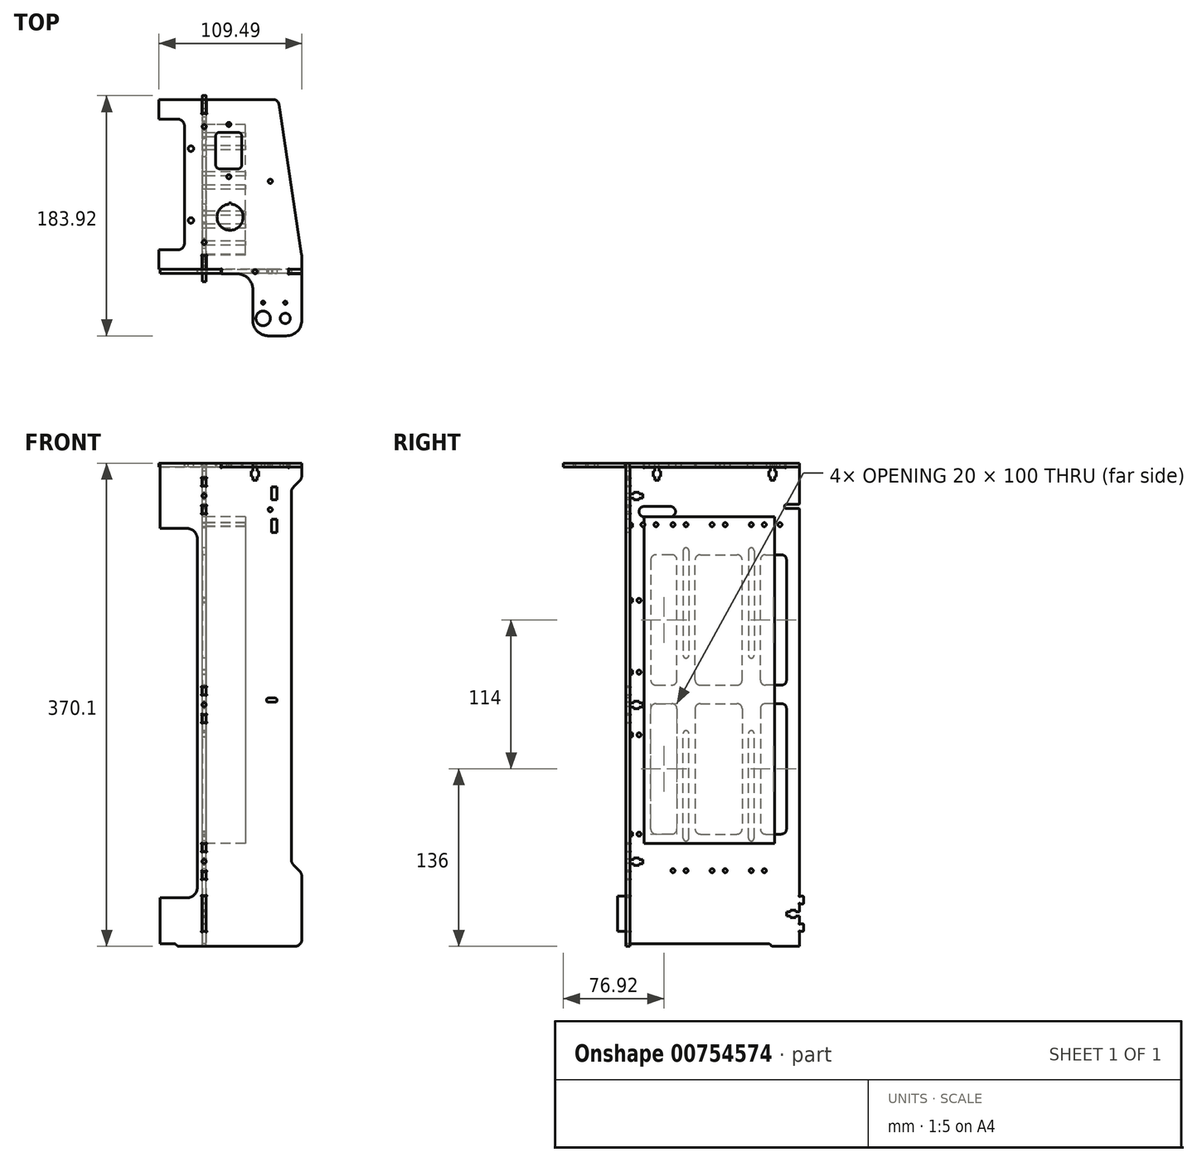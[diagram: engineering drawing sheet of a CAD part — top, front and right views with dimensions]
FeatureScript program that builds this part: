
annotation { "Feature Type Name" : "Feature", "Feature Type Description" : "" }
export const myFeature = defineFeature(function(context is Context, id is Id, definition is map)
    precondition{}
    {
        {
            assignVariable(context, id + "F0", {"name" : "profondeur_alim", "anyValue" : 30});
        }
        {
            var Q0;
            Q0=qCreatedBy(makeId("Top.planeOp"),FACE);
            var sketch = newSketch(context, id + "F1", { "sketchPlane" : qUnion([Q0])});
            skLineSegment(sketch, "E0", {"start": v(194.9, -37.1) * mm, "end": v(185.77, -37.1) * mm});
            skArc(sketch, "E1", {"start": v(185.33, -36.84) * mm, "mid": v(185.52, -37.03) * mm, "end": v(185.77, -37.1) * mm});
            skArc(sketch, "E2", {"start": v(185.33, -36.84) * mm, "mid": v(184.55, -36.74) * mm, "end": v(184.65, -37.53) * mm});
            skArc(sketch, "E3", {"start": v(184.9, -37.96) * mm, "mid": v(184.83, -37.71) * mm, "end": v(184.65, -37.53) * mm});
            skLineSegment(sketch, "E4", {"start": v(184.9, -37.96) * mm, "end": v(184.9, -39.53) * mm});
            skArc(sketch, "E5", {"start": v(184.65, -39.96) * mm, "mid": v(184.83, -39.78) * mm, "end": v(184.9, -39.53) * mm});
            skArc(sketch, "E6", {"start": v(184.65, -39.96) * mm, "mid": v(184.55, -40.75) * mm, "end": v(185.33, -40.64) * mm});
            skArc(sketch, "E7", {"start": v(185.77, -40.4) * mm, "mid": v(185.52, -40.46) * mm, "end": v(185.33, -40.64) * mm});
            skLineSegment(sketch, "E8", {"start": v(185.77, -40.4) * mm, "end": v(194.9, -40.4) * mm});
            skCircle(sketch, "E9", {"center": v(159.08, -38.74) * mm, "radius": 1.6 * mm});
            skLineSegment(sketch, "E10", {"start": v(133.25, -40.4) * mm, "end": v(133.25, -37.92) * mm});
            skArc(sketch, "E11", {"start": v(133.5, -37.48) * mm, "mid": v(133.32, -37.67) * mm, "end": v(133.25, -37.92) * mm});
            skArc(sketch, "E12", {"start": v(133.5, -37.48) * mm, "mid": v(133.6, -36.7) * mm, "end": v(132.82, -36.8) * mm});
            skArc(sketch, "E13", {"start": v(132.38, -37.05) * mm, "mid": v(132.63, -36.98) * mm, "end": v(132.82, -36.8) * mm});
            skLineSegment(sketch, "E14", {"start": v(132.38, -37.05) * mm, "end": v(121.73, -37.05) * mm});
            skLineSegment(sketch, "E15", {"start": v(121.73, -37.05) * mm, "end": v(121.73, -27.27) * mm});
            skArc(sketch, "E16", {"start": v(121.98, -26.83) * mm, "mid": v(121.8, -27.02) * mm, "end": v(121.73, -27.27) * mm});
            skArc(sketch, "E17", {"start": v(121.98, -26.83) * mm, "mid": v(122.08, -26.05) * mm, "end": v(121.3, -26.15) * mm});
            skArc(sketch, "E18", {"start": v(120.86, -26.4) * mm, "mid": v(121.1, -26.33) * mm, "end": v(121.3, -26.15) * mm});
            skLineSegment(sketch, "E19", {"start": v(120.86, -26.4) * mm, "end": v(119.3, -26.4) * mm});
            skArc(sketch, "E20", {"start": v(118.86, -26.15) * mm, "mid": v(119.04, -26.33) * mm, "end": v(119.3, -26.4) * mm});
            skArc(sketch, "E21", {"start": v(118.86, -26.15) * mm, "mid": v(118.07, -26.05) * mm, "end": v(118.18, -26.83) * mm});
            skArc(sketch, "E22", {"start": v(118.43, -27.27) * mm, "mid": v(118.36, -27.02) * mm, "end": v(118.18, -26.83) * mm});
            skLineSegment(sketch, "E23", {"start": v(118.43, -27.27) * mm, "end": v(118.43, -37.05) * mm});
            skCircle(sketch, "E24", {"center": v(120.08, -16.4) * mm, "radius": 1.6 * mm});
            skLineSegment(sketch, "E25", {"start": v(118.43, -37.05) * mm, "end": v(85.41, -37.05) * mm});
            skArc(sketch, "E26", {"start": v(99.9, -22.05) * mm, "mid": v(103.44, -20.58) * mm, "end": v(104.9, -17.05) * mm});
            skLineSegment(sketch, "E27", {"start": v(99.9, -22.05) * mm, "end": v(85.41, -22.05) * mm});
            skCircle(sketch, "E28", {"center": v(109.9, 0.45) * mm, "radius": 2.1 * mm});
            skLineSegment(sketch, "E29", {"start": v(194.9, -40.4) * mm, "end": v(194.9, -75.92) * mm});
            skArc(sketch, "E30", {"start": v(182.9, -87.92) * mm, "mid": v(191.39, -84.4) * mm, "end": v(194.9, -75.92) * mm});
            skCircle(sketch, "E31", {"center": v(182.2, -62.54) * mm, "radius": 1.25 * mm});
            skCircle(sketch, "E32", {"center": v(165.2, -74.55) * mm, "radius": 5.53 * mm});
            skCircle(sketch, "E33", {"center": v(165.2, -62.54) * mm, "radius": 1.25 * mm});
            skCircle(sketch, "E34", {"center": v(182.2, -74.54) * mm, "radius": 3.9 * mm});
            skLineSegment(sketch, "E35", {"start": v(194.9, -37.1) * mm, "end": v(194.9, -28.66) * mm});
            skArc(sketch, "E36", {"start": v(194.9, -28.66) * mm, "mid": v(194.84, -27.1) * mm, "end": v(194.66, -25.54) * mm});
            skCircle(sketch, "E37", {"center": v(120.08, 72.3) * mm, "radius": 1.6 * mm});
            skArc(sketch, "E38", {"start": v(104.9, 72.95) * mm, "mid": v(103.44, 76.49) * mm, "end": v(99.9, 77.95) * mm});
            skLineSegment(sketch, "E39", {"start": v(85.41, 77.95) * mm, "end": v(99.9, 77.95) * mm});
            skLineSegment(sketch, "E40", {"start": v(104.9, 72.95) * mm, "end": v(104.9, -17.05) * mm});
            skLineSegment(sketch, "E41", {"start": v(121.72, 92.95) * mm, "end": v(121.72, 83.17) * mm});
            skArc(sketch, "E42", {"start": v(121.72, 83.17) * mm, "mid": v(121.8, 82.92) * mm, "end": v(121.97, 82.73) * mm});
            skArc(sketch, "E43", {"start": v(121.3, 82.05) * mm, "mid": v(122.08, 81.95) * mm, "end": v(121.97, 82.73) * mm});
            skArc(sketch, "E44", {"start": v(121.3, 82.05) * mm, "mid": v(121.1, 82.23) * mm, "end": v(120.86, 82.3) * mm});
            skLineSegment(sketch, "E45", {"start": v(120.86, 82.3) * mm, "end": v(119.3, 82.3) * mm});
            skArc(sketch, "E46", {"start": v(119.3, 82.3) * mm, "mid": v(119.04, 82.23) * mm, "end": v(118.86, 82.05) * mm});
            skArc(sketch, "E47", {"start": v(118.17, 82.74) * mm, "mid": v(118.07, 81.95) * mm, "end": v(118.86, 82.05) * mm});
            skArc(sketch, "E48", {"start": v(118.17, 82.74) * mm, "mid": v(118.36, 82.92) * mm, "end": v(118.42, 83.17) * mm});
            skLineSegment(sketch, "E49", {"start": v(118.42, 83.17) * mm, "end": v(118.42, 92.95) * mm});
            skLineSegment(sketch, "E50", {"start": v(118.42, 92.95) * mm, "end": v(85.41, 92.95) * mm});
            skLineSegment(sketch, "E51", {"start": v(173.3, 92.95) * mm, "end": v(121.72, 92.95) * mm});
            skArc(sketch, "E52", {"start": v(177.26, 89.57) * mm, "mid": v(175.9, 92) * mm, "end": v(173.3, 92.95) * mm});
            skLineSegment(sketch, "E53", {"start": v(194.66, -25.54) * mm, "end": v(177.26, 89.57) * mm});
            skCircle(sketch, "E54", {"center": v(109.9, 55.45) * mm, "radius": 2.1 * mm});
            skArc(sketch, "E55", {"start": v(157.3, -52.4) * mm, "mid": v(153.78, -43.91) * mm, "end": v(145.29, -40.4) * mm});
            skArc(sketch, "E56", {"start": v(157.3, -75.92) * mm, "mid": v(160.8, -84.4) * mm, "end": v(169.3, -87.92) * mm});
            skLineSegment(sketch, "E57", {"start": v(157.3, -52.4) * mm, "end": v(157.3, -75.92) * mm});
            skLineSegment(sketch, "E58", {"start": v(145.29, -40.4) * mm, "end": v(133.25, -40.4) * mm});
            skLineSegment(sketch, "E59", {"start": v(169.3, -87.92) * mm, "end": v(182.9, -87.92) * mm});
            skCircle(sketch, "E60", {"center": v(138.87, 33.99) * mm, "radius": 1.6 * mm});
            skArc(sketch, "E61", {"start": v(145.87, 39.99) * mm, "mid": v(148, 40.87) * mm, "end": v(148.87, 42.99) * mm});
            skLineSegment(sketch, "E62", {"start": v(145.87, 39.99) * mm, "end": v(131.87, 39.99) * mm});
            skArc(sketch, "E63", {"start": v(128.87, 42.99) * mm, "mid": v(129.75, 40.87) * mm, "end": v(131.87, 39.99) * mm});
            skLineSegment(sketch, "E64", {"start": v(128.87, 64.99) * mm, "end": v(128.87, 42.99) * mm});
            skArc(sketch, "E65", {"start": v(131.87, 67.99) * mm, "mid": v(129.75, 67.1) * mm, "end": v(128.87, 64.99) * mm});
            skLineSegment(sketch, "E66", {"start": v(145.87, 67.99) * mm, "end": v(131.87, 67.99) * mm});
            skArc(sketch, "E67", {"start": v(148.87, 64.99) * mm, "mid": v(148, 67.1) * mm, "end": v(145.87, 67.99) * mm});
            skLineSegment(sketch, "E68", {"start": v(148.87, 64.99) * mm, "end": v(148.87, 42.99) * mm});
            skCircle(sketch, "E69", {"center": v(138.87, 73.99) * mm, "radius": 1.6 * mm});
            skArc(sketch, "E70", {"start": v(138.8, 12.89) * mm, "mid": v(139.9, -7.05) * mm, "end": v(141, 12.89) * mm});
            skLineSegment(sketch, "E71", {"start": v(141, 13.95) * mm, "end": v(141, 12.9) * mm});
            skLineSegment(sketch, "E72", {"start": v(138.8, 13.95) * mm, "end": v(138.8, 12.9) * mm});
            skLineSegment(sketch, "E73", {"start": v(138.8, 13.95) * mm, "end": v(141, 13.95) * mm});
            skCircle(sketch, "E74", {"center": v(170.72, 30.45) * mm, "radius": 1.6 * mm});
            skLineSegment(sketch, "E75", {"start": v(85.41, -37.05) * mm, "end": v(85.41, -22.05) * mm});
            skLineSegment(sketch, "E76", {"start": v(76.17, 13.3) * mm, "end": v(24.44, 13.3) * mm, "construction": true});
            skPoint(sketch, "E77.end.orphan", {"position": v(52.4, -36.45) * mm});
            skLineSegment(sketch, "E78.trimOffspring", {"start": v(85.41, 77.95) * mm, "end": v(85.41, 92.95) * mm});
            skSolve(sketch);
        }
        {
            var Q0;
            Q0=makeQuery(id+"F1.imprint","IMPRINT",FACE,{"disambiguationData":[TD([[makeQuery(id+"F1.imprint","IMPRINT",EDGE,{"derivedFrom":sQuery(id+"F1.wireOp",EDGE,"E0")}),-1.0]])]});
            extrude(context, id + "F2", {"entities" : qUnion([Q0]), "oppositeDirection" : true, "depth" : 3 * mm, "offsetDistance" : 25 * mm});
        }
        {
            var Q0;
            Q0=qCreatedBy(makeId("Front.planeOp"),FACE);
            cPlane(context, id + "F3", {"entities" : qUnion([Q0]), "cplaneType" : CPlaneType.OFFSET, "offset" : 40 * mm, "width" : 150 * mm, "height" : 150 * mm});
        }
        {
            var Q0;
            Q0=qCreatedBy(id+"F3.planeOp",FACE);
            var sketch = newSketch(context, id + "F4", { "sketchPlane" : qUnion([Q0])});
            skArc(sketch, "E79", {"start": v(189.8, -369.9) * mm, "mid": v(193.34, -368.44) * mm, "end": v(194.8, -364.9) * mm});
            skLineSegment(sketch, "E80", {"start": v(194.8, 0.1) * mm, "end": v(184.8, 0.1) * mm});
            skLineSegment(sketch, "E81", {"start": v(184.8, 0.1) * mm, "end": v(184.8, -2.13) * mm});
            skArc(sketch, "E82", {"start": v(184.8, -2.13) * mm, "mid": v(184.87, -2.38) * mm, "end": v(185.06, -2.57) * mm});
            skArc(sketch, "E83", {"start": v(184.37, -3.25) * mm, "mid": v(185.16, -3.35) * mm, "end": v(185.06, -2.57) * mm});
            skArc(sketch, "E84", {"start": v(184.37, -3.25) * mm, "mid": v(184.19, -3.07) * mm, "end": v(183.94, -3) * mm});
            skLineSegment(sketch, "E85", {"start": v(183.94, -3) * mm, "end": v(160.58, -3) * mm});
            skLineSegment(sketch, "E86", {"start": v(160.58, -3) * mm, "end": v(160.58, -6) * mm});
            skLineSegment(sketch, "E87", {"start": v(160.58, -6) * mm, "end": v(161.86, -6) * mm});
            skLineSegment(sketch, "E88", {"start": v(161.86, -6) * mm, "end": v(161.86, -10) * mm});
            skLineSegment(sketch, "E89", {"start": v(161.86, -10) * mm, "end": v(160.58, -10) * mm});
            skLineSegment(sketch, "E90", {"start": v(160.58, -10) * mm, "end": v(160.58, -13) * mm});
            skLineSegment(sketch, "E91", {"start": v(160.58, -13) * mm, "end": v(157.38, -13) * mm});
            skLineSegment(sketch, "E92", {"start": v(157.38, -13) * mm, "end": v(157.38, -10) * mm});
            skLineSegment(sketch, "E93", {"start": v(157.38, -10) * mm, "end": v(156.1, -10) * mm});
            skLineSegment(sketch, "E94", {"start": v(156.1, -10) * mm, "end": v(156.1, -6) * mm});
            skLineSegment(sketch, "E95", {"start": v(156.1, -6) * mm, "end": v(157.38, -6) * mm});
            skLineSegment(sketch, "E96", {"start": v(157.38, -6) * mm, "end": v(157.38, -3) * mm});
            skLineSegment(sketch, "E97", {"start": v(106.8, -49.9) * mm, "end": v(86.12, -49.9) * mm});
            skArc(sketch, "E98", {"start": v(120.76, -331.2) * mm, "mid": v(121.01, -331.13) * mm, "end": v(121.2, -330.95) * mm});
            skArc(sketch, "E99", {"start": v(121.88, -331.63) * mm, "mid": v(121.98, -330.85) * mm, "end": v(121.2, -330.95) * mm});
            skArc(sketch, "E100", {"start": v(121.88, -331.63) * mm, "mid": v(121.7, -331.82) * mm, "end": v(121.63, -332.07) * mm});
            skLineSegment(sketch, "E101", {"start": v(121.63, -332.07) * mm, "end": v(121.63, -357.73) * mm});
            skArc(sketch, "E102", {"start": v(121.63, -357.73) * mm, "mid": v(121.7, -357.98) * mm, "end": v(121.88, -358.17) * mm});
            skArc(sketch, "E103", {"start": v(121.2, -358.85) * mm, "mid": v(121.98, -358.95) * mm, "end": v(121.88, -358.17) * mm});
            skArc(sketch, "E104", {"start": v(121.2, -358.85) * mm, "mid": v(121.01, -358.67) * mm, "end": v(120.76, -358.6) * mm});
            skLineSegment(sketch, "E105", {"start": v(120.76, -358.6) * mm, "end": v(119.2, -358.6) * mm});
            skArc(sketch, "E106", {"start": v(119.2, -358.6) * mm, "mid": v(118.95, -358.67) * mm, "end": v(118.76, -358.85) * mm});
            skArc(sketch, "E107", {"start": v(118.08, -358.17) * mm, "mid": v(117.98, -358.95) * mm, "end": v(118.76, -358.85) * mm});
            skArc(sketch, "E108", {"start": v(118.08, -358.17) * mm, "mid": v(118.26, -357.98) * mm, "end": v(118.33, -357.73) * mm});
            skLineSegment(sketch, "E109", {"start": v(118.33, -357.73) * mm, "end": v(118.33, -332.07) * mm});
            skArc(sketch, "E110", {"start": v(118.33, -332.07) * mm, "mid": v(118.26, -331.82) * mm, "end": v(118.08, -331.63) * mm});
            skArc(sketch, "E111", {"start": v(118.76, -330.95) * mm, "mid": v(117.98, -330.85) * mm, "end": v(118.08, -331.63) * mm});
            skArc(sketch, "E112", {"start": v(118.76, -330.95) * mm, "mid": v(118.95, -331.13) * mm, "end": v(119.2, -331.2) * mm});
            skLineSegment(sketch, "E113", {"start": v(119.2, -331.2) * mm, "end": v(120.76, -331.2) * mm});
            skArc(sketch, "E114", {"start": v(118.76, -312.15) * mm, "mid": v(118.95, -312.33) * mm, "end": v(119.2, -312.4) * mm});
            skArc(sketch, "E115", {"start": v(118.76, -312.15) * mm, "mid": v(117.98, -312.05) * mm, "end": v(118.08, -312.83) * mm});
            skArc(sketch, "E116", {"start": v(118.33, -313.27) * mm, "mid": v(118.26, -313.02) * mm, "end": v(118.08, -312.83) * mm});
            skLineSegment(sketch, "E117", {"start": v(118.33, -313.27) * mm, "end": v(118.33, -317.73) * mm});
            skArc(sketch, "E118", {"start": v(118.08, -318.17) * mm, "mid": v(118.26, -317.98) * mm, "end": v(118.33, -317.73) * mm});
            skArc(sketch, "E119", {"start": v(118.08, -318.17) * mm, "mid": v(117.98, -318.95) * mm, "end": v(118.76, -318.85) * mm});
            skArc(sketch, "E120", {"start": v(119.2, -318.6) * mm, "mid": v(118.95, -318.67) * mm, "end": v(118.76, -318.85) * mm});
            skLineSegment(sketch, "E121", {"start": v(119.2, -318.6) * mm, "end": v(120.76, -318.6) * mm});
            skArc(sketch, "E122", {"start": v(121.2, -318.85) * mm, "mid": v(121.01, -318.67) * mm, "end": v(120.76, -318.6) * mm});
            skArc(sketch, "E123", {"start": v(121.2, -318.85) * mm, "mid": v(121.98, -318.95) * mm, "end": v(121.88, -318.17) * mm});
            skArc(sketch, "E124", {"start": v(121.63, -317.73) * mm, "mid": v(121.7, -317.98) * mm, "end": v(121.88, -318.17) * mm});
            skLineSegment(sketch, "E125", {"start": v(121.63, -317.73) * mm, "end": v(121.63, -313.27) * mm});
            skArc(sketch, "E126", {"start": v(121.88, -312.83) * mm, "mid": v(121.7, -313.02) * mm, "end": v(121.63, -313.27) * mm});
            skArc(sketch, "E127", {"start": v(121.88, -312.83) * mm, "mid": v(121.98, -312.05) * mm, "end": v(121.2, -312.15) * mm});
            skArc(sketch, "E128", {"start": v(120.76, -312.4) * mm, "mid": v(121.01, -312.33) * mm, "end": v(121.2, -312.15) * mm});
            skLineSegment(sketch, "E129", {"start": v(120.76, -312.4) * mm, "end": v(119.2, -312.4) * mm});
            skArc(sketch, "E130", {"start": v(118.76, -290.95) * mm, "mid": v(118.95, -291.13) * mm, "end": v(119.2, -291.2) * mm});
            skArc(sketch, "E131", {"start": v(118.76, -290.95) * mm, "mid": v(117.98, -290.85) * mm, "end": v(118.08, -291.63) * mm});
            skArc(sketch, "E132", {"start": v(118.33, -292.07) * mm, "mid": v(118.26, -291.82) * mm, "end": v(118.08, -291.63) * mm});
            skLineSegment(sketch, "E133", {"start": v(118.33, -292.07) * mm, "end": v(118.33, -296.53) * mm});
            skArc(sketch, "E134", {"start": v(118.08, -296.97) * mm, "mid": v(118.26, -296.78) * mm, "end": v(118.33, -296.53) * mm});
            skArc(sketch, "E135", {"start": v(118.08, -296.97) * mm, "mid": v(117.98, -297.75) * mm, "end": v(118.76, -297.65) * mm});
            skArc(sketch, "E136", {"start": v(119.2, -297.4) * mm, "mid": v(118.95, -297.47) * mm, "end": v(118.76, -297.65) * mm});
            skLineSegment(sketch, "E137", {"start": v(119.2, -297.4) * mm, "end": v(120.76, -297.4) * mm});
            skArc(sketch, "E138", {"start": v(121.2, -297.65) * mm, "mid": v(121.01, -297.47) * mm, "end": v(120.76, -297.4) * mm});
            skArc(sketch, "E139", {"start": v(121.2, -297.65) * mm, "mid": v(121.98, -297.75) * mm, "end": v(121.88, -296.97) * mm});
            skArc(sketch, "E140", {"start": v(121.63, -296.53) * mm, "mid": v(121.7, -296.78) * mm, "end": v(121.88, -296.97) * mm});
            skLineSegment(sketch, "E141", {"start": v(121.63, -296.53) * mm, "end": v(121.63, -292.07) * mm});
            skArc(sketch, "E142", {"start": v(121.88, -291.63) * mm, "mid": v(121.7, -291.82) * mm, "end": v(121.63, -292.07) * mm});
            skArc(sketch, "E143", {"start": v(121.88, -291.63) * mm, "mid": v(121.98, -290.85) * mm, "end": v(121.2, -290.95) * mm});
            skArc(sketch, "E144", {"start": v(120.76, -291.2) * mm, "mid": v(121.01, -291.13) * mm, "end": v(121.2, -290.95) * mm});
            skLineSegment(sketch, "E145", {"start": v(120.76, -291.2) * mm, "end": v(119.2, -291.2) * mm});
            skArc(sketch, "E146", {"start": v(120.76, -192.4) * mm, "mid": v(121.01, -192.33) * mm, "end": v(121.2, -192.15) * mm});
            skArc(sketch, "E147", {"start": v(121.88, -192.83) * mm, "mid": v(121.98, -192.05) * mm, "end": v(121.2, -192.15) * mm});
            skArc(sketch, "E148", {"start": v(121.88, -192.83) * mm, "mid": v(121.7, -193.02) * mm, "end": v(121.63, -193.27) * mm});
            skLineSegment(sketch, "E149", {"start": v(121.63, -193.27) * mm, "end": v(121.63, -197.73) * mm});
            skArc(sketch, "E150", {"start": v(121.63, -197.73) * mm, "mid": v(121.7, -197.98) * mm, "end": v(121.88, -198.17) * mm});
            skArc(sketch, "E151", {"start": v(121.2, -198.85) * mm, "mid": v(121.98, -198.95) * mm, "end": v(121.88, -198.17) * mm});
            skArc(sketch, "E152", {"start": v(121.2, -198.85) * mm, "mid": v(121.01, -198.67) * mm, "end": v(120.76, -198.6) * mm});
            skLineSegment(sketch, "E153", {"start": v(120.76, -198.6) * mm, "end": v(119.2, -198.6) * mm});
            skArc(sketch, "E154", {"start": v(119.2, -198.6) * mm, "mid": v(118.95, -198.67) * mm, "end": v(118.76, -198.85) * mm});
            skArc(sketch, "E155", {"start": v(118.08, -198.17) * mm, "mid": v(117.98, -198.95) * mm, "end": v(118.76, -198.85) * mm});
            skArc(sketch, "E156", {"start": v(118.08, -198.17) * mm, "mid": v(118.26, -197.98) * mm, "end": v(118.33, -197.73) * mm});
            skLineSegment(sketch, "E157", {"start": v(118.33, -197.73) * mm, "end": v(118.33, -193.27) * mm});
            skArc(sketch, "E158", {"start": v(118.33, -193.27) * mm, "mid": v(118.26, -193.02) * mm, "end": v(118.08, -192.83) * mm});
            skArc(sketch, "E159", {"start": v(118.76, -192.15) * mm, "mid": v(117.98, -192.05) * mm, "end": v(118.08, -192.83) * mm});
            skArc(sketch, "E160", {"start": v(118.76, -192.15) * mm, "mid": v(118.95, -192.33) * mm, "end": v(119.2, -192.4) * mm});
            skLineSegment(sketch, "E161", {"start": v(119.2, -192.4) * mm, "end": v(120.76, -192.4) * mm});
            skArc(sketch, "E162", {"start": v(120.76, -171.2) * mm, "mid": v(121.01, -171.13) * mm, "end": v(121.2, -170.95) * mm});
            skArc(sketch, "E163", {"start": v(121.88, -171.63) * mm, "mid": v(121.98, -170.85) * mm, "end": v(121.2, -170.95) * mm});
            skArc(sketch, "E164", {"start": v(121.88, -171.63) * mm, "mid": v(121.7, -171.82) * mm, "end": v(121.63, -172.07) * mm});
            skLineSegment(sketch, "E165", {"start": v(121.63, -172.07) * mm, "end": v(121.63, -176.53) * mm});
            skArc(sketch, "E166", {"start": v(121.63, -176.53) * mm, "mid": v(121.7, -176.78) * mm, "end": v(121.88, -176.97) * mm});
            skArc(sketch, "E167", {"start": v(121.2, -177.65) * mm, "mid": v(121.98, -177.75) * mm, "end": v(121.88, -176.97) * mm});
            skArc(sketch, "E168", {"start": v(121.2, -177.65) * mm, "mid": v(121.01, -177.47) * mm, "end": v(120.76, -177.4) * mm});
            skLineSegment(sketch, "E169", {"start": v(120.76, -177.4) * mm, "end": v(119.2, -177.4) * mm});
            skArc(sketch, "E170", {"start": v(119.2, -177.4) * mm, "mid": v(118.95, -177.47) * mm, "end": v(118.76, -177.65) * mm});
            skArc(sketch, "E171", {"start": v(118.08, -176.97) * mm, "mid": v(117.98, -177.75) * mm, "end": v(118.76, -177.65) * mm});
            skArc(sketch, "E172", {"start": v(118.08, -176.97) * mm, "mid": v(118.26, -176.78) * mm, "end": v(118.33, -176.53) * mm});
            skLineSegment(sketch, "E173", {"start": v(118.33, -176.53) * mm, "end": v(118.33, -172.07) * mm});
            skArc(sketch, "E174", {"start": v(118.33, -172.07) * mm, "mid": v(118.26, -171.82) * mm, "end": v(118.08, -171.63) * mm});
            skArc(sketch, "E175", {"start": v(118.76, -170.95) * mm, "mid": v(117.98, -170.85) * mm, "end": v(118.08, -171.63) * mm});
            skArc(sketch, "E176", {"start": v(118.76, -170.95) * mm, "mid": v(118.95, -171.13) * mm, "end": v(119.2, -171.2) * mm});
            skLineSegment(sketch, "E177", {"start": v(119.2, -171.2) * mm, "end": v(120.76, -171.2) * mm});
            skArc(sketch, "E178", {"start": v(120.76, -32.4) * mm, "mid": v(121.01, -32.33) * mm, "end": v(121.2, -32.15) * mm});
            skArc(sketch, "E179", {"start": v(121.88, -32.83) * mm, "mid": v(121.98, -32.05) * mm, "end": v(121.2, -32.15) * mm});
            skArc(sketch, "E180", {"start": v(121.88, -32.83) * mm, "mid": v(121.7, -33.02) * mm, "end": v(121.63, -33.27) * mm});
            skLineSegment(sketch, "E181", {"start": v(121.63, -33.27) * mm, "end": v(121.63, -37.73) * mm});
            skArc(sketch, "E182", {"start": v(121.63, -37.73) * mm, "mid": v(121.7, -37.98) * mm, "end": v(121.88, -38.17) * mm});
            skArc(sketch, "E183", {"start": v(121.2, -38.85) * mm, "mid": v(121.98, -38.95) * mm, "end": v(121.88, -38.17) * mm});
            skArc(sketch, "E184", {"start": v(121.2, -38.85) * mm, "mid": v(121.01, -38.67) * mm, "end": v(120.76, -38.6) * mm});
            skLineSegment(sketch, "E185", {"start": v(120.76, -38.6) * mm, "end": v(119.2, -38.6) * mm});
            skArc(sketch, "E186", {"start": v(119.2, -38.6) * mm, "mid": v(118.95, -38.67) * mm, "end": v(118.76, -38.85) * mm});
            skArc(sketch, "E187", {"start": v(118.08, -38.17) * mm, "mid": v(117.98, -38.95) * mm, "end": v(118.76, -38.85) * mm});
            skArc(sketch, "E188", {"start": v(118.08, -38.17) * mm, "mid": v(118.26, -37.98) * mm, "end": v(118.33, -37.73) * mm});
            skLineSegment(sketch, "E189", {"start": v(118.33, -37.73) * mm, "end": v(118.33, -33.27) * mm});
            skArc(sketch, "E190", {"start": v(118.33, -33.27) * mm, "mid": v(118.26, -33.02) * mm, "end": v(118.08, -32.83) * mm});
            skArc(sketch, "E191", {"start": v(118.76, -32.15) * mm, "mid": v(117.98, -32.05) * mm, "end": v(118.08, -32.83) * mm});
            skArc(sketch, "E192", {"start": v(118.76, -32.15) * mm, "mid": v(118.95, -32.33) * mm, "end": v(119.2, -32.4) * mm});
            skLineSegment(sketch, "E193", {"start": v(119.2, -32.4) * mm, "end": v(120.76, -32.4) * mm});
            skArc(sketch, "E194", {"start": v(120.76, -11.2) * mm, "mid": v(121.01, -11.13) * mm, "end": v(121.2, -10.95) * mm});
            skArc(sketch, "E195", {"start": v(121.88, -11.63) * mm, "mid": v(121.98, -10.85) * mm, "end": v(121.2, -10.95) * mm});
            skArc(sketch, "E196", {"start": v(121.88, -11.63) * mm, "mid": v(121.7, -11.82) * mm, "end": v(121.63, -12.07) * mm});
            skLineSegment(sketch, "E197", {"start": v(121.63, -12.07) * mm, "end": v(121.63, -16.53) * mm});
            skArc(sketch, "E198", {"start": v(121.63, -16.53) * mm, "mid": v(121.7, -16.78) * mm, "end": v(121.88, -16.97) * mm});
            skArc(sketch, "E199", {"start": v(121.2, -17.65) * mm, "mid": v(121.98, -17.75) * mm, "end": v(121.88, -16.97) * mm});
            skArc(sketch, "E200", {"start": v(121.2, -17.65) * mm, "mid": v(121.01, -17.47) * mm, "end": v(120.76, -17.4) * mm});
            skLineSegment(sketch, "E201", {"start": v(120.76, -17.4) * mm, "end": v(119.2, -17.4) * mm});
            skArc(sketch, "E202", {"start": v(119.2, -17.4) * mm, "mid": v(118.95, -17.47) * mm, "end": v(118.76, -17.65) * mm});
            skArc(sketch, "E203", {"start": v(118.08, -16.97) * mm, "mid": v(117.98, -17.75) * mm, "end": v(118.76, -17.65) * mm});
            skArc(sketch, "E204", {"start": v(118.08, -16.97) * mm, "mid": v(118.26, -16.78) * mm, "end": v(118.33, -16.53) * mm});
            skLineSegment(sketch, "E205", {"start": v(118.33, -16.53) * mm, "end": v(118.33, -12.07) * mm});
            skArc(sketch, "E206", {"start": v(118.33, -12.07) * mm, "mid": v(118.26, -11.82) * mm, "end": v(118.08, -11.63) * mm});
            skArc(sketch, "E207", {"start": v(118.76, -10.95) * mm, "mid": v(117.98, -10.85) * mm, "end": v(118.08, -11.63) * mm});
            skArc(sketch, "E208", {"start": v(118.76, -10.95) * mm, "mid": v(118.95, -11.13) * mm, "end": v(119.2, -11.2) * mm});
            skLineSegment(sketch, "E209", {"start": v(119.2, -11.2) * mm, "end": v(120.76, -11.2) * mm});
            skCircle(sketch, "E210", {"center": v(119.98, -304.9) * mm, "radius": 1.6 * mm});
            skCircle(sketch, "E211", {"center": v(119.98, -184.9) * mm, "radius": 1.6 * mm});
            skCircle(sketch, "E212", {"center": v(119.98, -24.9) * mm, "radius": 1.6 * mm});
            skLineSegment(sketch, "E213", {"start": v(114.8, -324.8) * mm, "end": v(114.8, -57.9) * mm});
            skArc(sketch, "E214", {"start": v(106.8, -332.78) * mm, "mid": v(112.46, -330.44) * mm, "end": v(114.8, -324.8) * mm});
            skLineSegment(sketch, "E215", {"start": v(133, 0.1) * mm, "end": v(86.12, 0.1) * mm});
            skArc(sketch, "E216", {"start": v(133.87, -3) * mm, "mid": v(133.62, -3.07) * mm, "end": v(133.44, -3.25) * mm});
            skArc(sketch, "E217", {"start": v(132.76, -2.57) * mm, "mid": v(132.65, -3.35) * mm, "end": v(133.44, -3.25) * mm});
            skArc(sketch, "E218", {"start": v(132.76, -2.57) * mm, "mid": v(132.94, -2.38) * mm, "end": v(133, -2.13) * mm});
            skLineSegment(sketch, "E219", {"start": v(133, -2.13) * mm, "end": v(133, 0.1) * mm});
            skLineSegment(sketch, "E220", {"start": v(157.38, -3) * mm, "end": v(133.87, -3) * mm});
            skLineSegment(sketch, "E221", {"start": v(194.8, -364.9) * mm, "end": v(194.8, -316.36) * mm});
            skArc(sketch, "E222", {"start": v(194.8, -316.36) * mm, "mid": v(194.36, -314.09) * mm, "end": v(193.07, -312.15) * mm});
            skLineSegment(sketch, "E223", {"start": v(188.54, -307.56) * mm, "end": v(193.07, -312.15) * mm});
            skArc(sketch, "E224", {"start": v(186.8, -303.34) * mm, "mid": v(187.26, -305.62) * mm, "end": v(188.54, -307.56) * mm});
            skLineSegment(sketch, "E225", {"start": v(194.8, -9.42) * mm, "end": v(194.8, 0.1) * mm});
            skArc(sketch, "E226", {"start": v(193.05, -13.66) * mm, "mid": v(194.35, -11.71) * mm, "end": v(194.8, -9.42) * mm});
            skLineSegment(sketch, "E227", {"start": v(193.05, -13.66) * mm, "end": v(188.56, -18.14) * mm});
            skArc(sketch, "E228", {"start": v(188.56, -18.14) * mm, "mid": v(187.26, -20.09) * mm, "end": v(186.8, -22.39) * mm});
            skLineSegment(sketch, "E229", {"start": v(106.8, -332.78) * mm, "end": v(86.12, -332.78) * mm});
            skArc(sketch, "E230", {"start": v(98.1, -368.2) * mm, "mid": v(97.77, -367.98) * mm, "end": v(97.4, -367.9) * mm});
            skLineSegment(sketch, "E231", {"start": v(189.8, -369.9) * mm, "end": v(100.22, -369.9) * mm});
            skLineSegment(sketch, "E232", {"start": v(98.1, -368.2) * mm, "end": v(99.51, -369.6) * mm});
            skArc(sketch, "E233", {"start": v(99.51, -369.6) * mm, "mid": v(99.84, -369.82) * mm, "end": v(100.22, -369.9) * mm});
            skArc(sketch, "E234", {"start": v(174.3, -183) * mm, "mid": v(175.9, -181.4) * mm, "end": v(174.3, -179.8) * mm});
            skArc(sketch, "E235", {"start": v(169.3, -179.8) * mm, "mid": v(167.7, -181.4) * mm, "end": v(169.3, -183) * mm});
            skLineSegment(sketch, "E236", {"start": v(174.3, -179.8) * mm, "end": v(169.3, -179.8) * mm});
            skLineSegment(sketch, "E237", {"start": v(174.3, -183) * mm, "end": v(169.3, -183) * mm});
            skLineSegment(sketch, "E238", {"start": v(186.8, -22.39) * mm, "end": v(186.8, -303.34) * mm});
            skLineSegment(sketch, "E239", {"start": v(171.63, -28) * mm, "end": v(171.63, -18) * mm});
            skLineSegment(sketch, "E240", {"start": v(171.63, -18) * mm, "end": v(175.63, -18) * mm});
            skLineSegment(sketch, "E241", {"start": v(175.63, -18) * mm, "end": v(175.63, -28) * mm});
            skLineSegment(sketch, "E242", {"start": v(175.63, -28) * mm, "end": v(171.63, -28) * mm});
            skLineSegment(sketch, "E243", {"start": v(171.63, -53) * mm, "end": v(171.63, -43) * mm});
            skLineSegment(sketch, "E244", {"start": v(171.63, -43) * mm, "end": v(175.63, -43) * mm});
            skLineSegment(sketch, "E245", {"start": v(175.63, -43) * mm, "end": v(175.63, -53) * mm});
            skLineSegment(sketch, "E246", {"start": v(175.63, -53) * mm, "end": v(171.63, -53) * mm});
            skCircle(sketch, "E247", {"center": v(170.63, -35.5) * mm, "radius": 1.6 * mm});
            skPoint(sketch, "E248.end.orphan", {"position": v(-11.92, 174.3) * mm});
            skPoint(sketch, "E249.end.orphan", {"position": v(92.12, 0.1) * mm});
            skLineSegment(sketch, "E250", {"start": v(86.12, -367.9) * mm, "end": v(97.4, -367.9) * mm});
            skLineSegment(sketch, "E251", {"start": v(86.12, -367.9) * mm, "end": v(86.12, -332.78) * mm});
            skPoint(sketch, "E252.orphan", {"position": v(125.38, -49.9) * mm});
            skLineSegment(sketch, "E253", {"start": v(86.12, -49.9) * mm, "end": v(86.12, 0.1) * mm});
            skPoint(sketch, "E254.end.orphan", {"position": v(96.46, -49.9) * mm});
            skArc(sketch, "E255", {"start": v(114.8, -57.9) * mm, "mid": v(112.46, -52.24) * mm, "end": v(106.8, -49.9) * mm});
            skSolve(sketch);
        }
        {
            var Q0;
            Q0=makeQuery(id+"F4.imprint","IMPRINT",FACE,{"disambiguationData":[TD([[makeQuery(id+"F4.imprint","IMPRINT",EDGE,{"derivedFrom":sQuery(id+"F4.wireOp",EDGE,"E79")}),1.0]])]});
            extrude(context, id + "F5", {"entities" : qUnion([Q0]), "operationType" : NewBodyOperationType.ADD, "oppositeDirection" : true, "depth" : 3 * mm, "offsetDistance" : 25 * mm});
        }
        {
            var Q0;
            Q0=qCreatedBy(makeId("Right.planeOp"),FACE);
            cPlane(context, id + "F6", {"entities" : qUnion([Q0]), "cplaneType" : CPlaneType.OFFSET, "offset" : 118.6 * mm, "width" : 150 * mm, "height" : 150 * mm});
        }
        {
            var Q0;
            Q0=qCreatedBy(id+"F6.planeOp",FACE);
            var sketch = newSketch(context, id + "F7", { "sketchPlane" : qUnion([Q0])});
            skLineSegment(sketch, "E256", {"start": v(-37, -368) * mm, "end": v(-37, -359.47) * mm});
            skArc(sketch, "E257", {"start": v(-36.75, -359.03) * mm, "mid": v(-36.93, -359.22) * mm, "end": v(-37, -359.47) * mm});
            skArc(sketch, "E258", {"start": v(-36.75, -359.03) * mm, "mid": v(-36.65, -358.25) * mm, "end": v(-37.43, -358.35) * mm});
            skArc(sketch, "E259", {"start": v(-37.87, -358.6) * mm, "mid": v(-37.62, -358.53) * mm, "end": v(-37.43, -358.35) * mm});
            skArc(sketch, "E260", {"start": v(-37.43, -331.65) * mm, "mid": v(-37.62, -331.47) * mm, "end": v(-37.87, -331.4) * mm});
            skArc(sketch, "E261", {"start": v(-37.43, -331.65) * mm, "mid": v(-36.65, -331.75) * mm, "end": v(-36.75, -330.97) * mm});
            skArc(sketch, "E262", {"start": v(-37, -330.53) * mm, "mid": v(-36.93, -330.78) * mm, "end": v(-36.75, -330.97) * mm});
            skLineSegment(sketch, "E263", {"start": v(-37, -330.53) * mm, "end": v(-37, -319.47) * mm});
            skArc(sketch, "E264", {"start": v(-36.75, -319.03) * mm, "mid": v(-36.93, -319.22) * mm, "end": v(-37, -319.47) * mm});
            skArc(sketch, "E265", {"start": v(-36.75, -319.03) * mm, "mid": v(-36.65, -318.25) * mm, "end": v(-37.43, -318.35) * mm});
            skArc(sketch, "E266", {"start": v(-37.87, -318.6) * mm, "mid": v(-37.62, -318.53) * mm, "end": v(-37.43, -318.35) * mm});
            skLineSegment(sketch, "E267", {"start": v(-37.87, -318.6) * mm, "end": v(-39.5, -318.6) * mm});
            skArc(sketch, "E268", {"start": v(-40, -318.1) * mm, "mid": v(-39.85, -318.45) * mm, "end": v(-39.5, -318.6) * mm});
            skLineSegment(sketch, "E269", {"start": v(-40, -318.1) * mm, "end": v(-40, -313.1) * mm});
            skArc(sketch, "E270", {"start": v(-39.5, -312.6) * mm, "mid": v(-39.85, -312.75) * mm, "end": v(-40, -313.1) * mm});
            skLineSegment(sketch, "E271", {"start": v(-39.5, -312.6) * mm, "end": v(-37.87, -312.6) * mm});
            skArc(sketch, "E272", {"start": v(-37.43, -312.85) * mm, "mid": v(-37.62, -312.67) * mm, "end": v(-37.87, -312.6) * mm});
            skArc(sketch, "E273", {"start": v(-37.43, -312.85) * mm, "mid": v(-36.65, -312.95) * mm, "end": v(-36.75, -312.17) * mm});
            skArc(sketch, "E274", {"start": v(-37, -311.73) * mm, "mid": v(-36.93, -311.98) * mm, "end": v(-36.75, -312.17) * mm});
            skLineSegment(sketch, "E275", {"start": v(-37, -311.73) * mm, "end": v(-37, -306.6) * mm});
            skLineSegment(sketch, "E276", {"start": v(-37, -306.6) * mm, "end": v(-34, -306.6) * mm});
            skLineSegment(sketch, "E277", {"start": v(-34, -306.6) * mm, "end": v(-34, -307.88) * mm});
            skLineSegment(sketch, "E278", {"start": v(-34, -307.88) * mm, "end": v(-30, -307.88) * mm});
            skLineSegment(sketch, "E279", {"start": v(-30, -307.88) * mm, "end": v(-30, -306.6) * mm});
            skLineSegment(sketch, "E280", {"start": v(-30, -306.6) * mm, "end": v(-27, -306.6) * mm});
            skLineSegment(sketch, "E281", {"start": v(-27, -306.6) * mm, "end": v(-27, -303.4) * mm});
            skLineSegment(sketch, "E282", {"start": v(-27, -303.4) * mm, "end": v(-30, -303.4) * mm});
            skLineSegment(sketch, "E283", {"start": v(-30, -303.4) * mm, "end": v(-30, -302.13) * mm});
            skLineSegment(sketch, "E284", {"start": v(-30, -302.13) * mm, "end": v(-34, -302.13) * mm});
            skLineSegment(sketch, "E285", {"start": v(-34, -302.13) * mm, "end": v(-34, -303.4) * mm});
            skLineSegment(sketch, "E286", {"start": v(-34, -303.4) * mm, "end": v(-37, -303.4) * mm});
            skLineSegment(sketch, "E287", {"start": v(-37, -303.4) * mm, "end": v(-37, -298.27) * mm});
            skArc(sketch, "E288", {"start": v(-36.75, -297.83) * mm, "mid": v(-36.93, -298.02) * mm, "end": v(-37, -298.27) * mm});
            skArc(sketch, "E289", {"start": v(-36.75, -297.83) * mm, "mid": v(-36.65, -297.05) * mm, "end": v(-37.43, -297.15) * mm});
            skArc(sketch, "E290", {"start": v(-37.87, -297.4) * mm, "mid": v(-37.62, -297.33) * mm, "end": v(-37.43, -297.15) * mm});
            skLineSegment(sketch, "E291", {"start": v(-37.87, -297.4) * mm, "end": v(-39.5, -297.4) * mm});
            skArc(sketch, "E292", {"start": v(-40, -296.9) * mm, "mid": v(-39.85, -297.25) * mm, "end": v(-39.5, -297.4) * mm});
            skLineSegment(sketch, "E293", {"start": v(-40, -296.9) * mm, "end": v(-40, -291.9) * mm});
            skArc(sketch, "E294", {"start": v(-39.5, -291.4) * mm, "mid": v(-39.85, -291.55) * mm, "end": v(-40, -291.9) * mm});
            skLineSegment(sketch, "E295", {"start": v(-39.5, -291.4) * mm, "end": v(-37.87, -291.4) * mm});
            skArc(sketch, "E296", {"start": v(-37.43, -291.65) * mm, "mid": v(-37.62, -291.47) * mm, "end": v(-37.87, -291.4) * mm});
            skArc(sketch, "E297", {"start": v(-37.43, -291.65) * mm, "mid": v(-36.65, -291.75) * mm, "end": v(-36.75, -290.97) * mm});
            skArc(sketch, "E298", {"start": v(-37, -290.53) * mm, "mid": v(-36.93, -290.78) * mm, "end": v(-36.75, -290.97) * mm});
            skArc(sketch, "E299", {"start": v(-36.75, -199.03) * mm, "mid": v(-36.93, -199.22) * mm, "end": v(-37, -199.47) * mm});
            skArc(sketch, "E300", {"start": v(-36.75, -199.03) * mm, "mid": v(-36.65, -198.25) * mm, "end": v(-37.43, -198.35) * mm});
            skArc(sketch, "E301", {"start": v(-37.87, -198.6) * mm, "mid": v(-37.62, -198.53) * mm, "end": v(-37.43, -198.35) * mm});
            skLineSegment(sketch, "E302", {"start": v(-37.87, -198.6) * mm, "end": v(-39.5, -198.6) * mm});
            skArc(sketch, "E303", {"start": v(-40, -198.1) * mm, "mid": v(-39.85, -198.45) * mm, "end": v(-39.5, -198.6) * mm});
            skLineSegment(sketch, "E304", {"start": v(-40, -198.1) * mm, "end": v(-40, -193.1) * mm});
            skArc(sketch, "E305", {"start": v(-39.5, -192.6) * mm, "mid": v(-39.85, -192.75) * mm, "end": v(-40, -193.1) * mm});
            skLineSegment(sketch, "E306", {"start": v(-39.5, -192.6) * mm, "end": v(-37.87, -192.6) * mm});
            skArc(sketch, "E307", {"start": v(-37.43, -192.85) * mm, "mid": v(-37.62, -192.67) * mm, "end": v(-37.87, -192.6) * mm});
            skArc(sketch, "E308", {"start": v(-37.43, -192.85) * mm, "mid": v(-36.65, -192.95) * mm, "end": v(-36.75, -192.17) * mm});
            skArc(sketch, "E309", {"start": v(-37, -191.73) * mm, "mid": v(-36.93, -191.98) * mm, "end": v(-36.75, -192.17) * mm});
            skLineSegment(sketch, "E310", {"start": v(-37, -191.73) * mm, "end": v(-37, -186.6) * mm});
            skLineSegment(sketch, "E311", {"start": v(-37, -186.6) * mm, "end": v(-34, -186.6) * mm});
            skLineSegment(sketch, "E312", {"start": v(-34, -186.6) * mm, "end": v(-34, -187.88) * mm});
            skLineSegment(sketch, "E313", {"start": v(-34, -187.88) * mm, "end": v(-30, -187.88) * mm});
            skLineSegment(sketch, "E314", {"start": v(-30, -187.88) * mm, "end": v(-30, -186.6) * mm});
            skLineSegment(sketch, "E315", {"start": v(-30, -186.6) * mm, "end": v(-27, -186.6) * mm});
            skLineSegment(sketch, "E316", {"start": v(-27, -186.6) * mm, "end": v(-27, -183.4) * mm});
            skLineSegment(sketch, "E317", {"start": v(-27, -183.4) * mm, "end": v(-30, -183.4) * mm});
            skLineSegment(sketch, "E318", {"start": v(-30, -183.4) * mm, "end": v(-30, -182.13) * mm});
            skLineSegment(sketch, "E319", {"start": v(-30, -182.13) * mm, "end": v(-34, -182.13) * mm});
            skLineSegment(sketch, "E320", {"start": v(-34, -182.13) * mm, "end": v(-34, -183.4) * mm});
            skLineSegment(sketch, "E321", {"start": v(-34, -183.4) * mm, "end": v(-37, -183.4) * mm});
            skLineSegment(sketch, "E322", {"start": v(-37, -183.4) * mm, "end": v(-37, -178.27) * mm});
            skArc(sketch, "E323", {"start": v(-36.75, -177.83) * mm, "mid": v(-36.93, -178.02) * mm, "end": v(-37, -178.27) * mm});
            skArc(sketch, "E324", {"start": v(-36.75, -177.83) * mm, "mid": v(-36.65, -177.05) * mm, "end": v(-37.43, -177.15) * mm});
            skArc(sketch, "E325", {"start": v(-37.87, -177.4) * mm, "mid": v(-37.62, -177.33) * mm, "end": v(-37.43, -177.15) * mm});
            skLineSegment(sketch, "E326", {"start": v(-37.87, -177.4) * mm, "end": v(-39.5, -177.4) * mm});
            skArc(sketch, "E327", {"start": v(-40, -176.9) * mm, "mid": v(-39.85, -177.25) * mm, "end": v(-39.5, -177.4) * mm});
            skLineSegment(sketch, "E328", {"start": v(-40, -176.9) * mm, "end": v(-40, -171.9) * mm});
            skArc(sketch, "E329", {"start": v(-39.5, -171.4) * mm, "mid": v(-39.85, -171.55) * mm, "end": v(-40, -171.9) * mm});
            skLineSegment(sketch, "E330", {"start": v(-39.5, -171.4) * mm, "end": v(-37.87, -171.4) * mm});
            skArc(sketch, "E331", {"start": v(-37.43, -171.65) * mm, "mid": v(-37.62, -171.47) * mm, "end": v(-37.87, -171.4) * mm});
            skArc(sketch, "E332", {"start": v(-37.43, -171.65) * mm, "mid": v(-36.65, -171.75) * mm, "end": v(-36.75, -170.97) * mm});
            skArc(sketch, "E333", {"start": v(-37, -170.53) * mm, "mid": v(-36.93, -170.78) * mm, "end": v(-36.75, -170.97) * mm});
            skArc(sketch, "E334", {"start": v(-36.75, -39.03) * mm, "mid": v(-36.93, -39.22) * mm, "end": v(-37, -39.47) * mm});
            skArc(sketch, "E335", {"start": v(-36.75, -39.03) * mm, "mid": v(-36.65, -38.25) * mm, "end": v(-37.43, -38.35) * mm});
            skArc(sketch, "E336", {"start": v(-37.87, -38.6) * mm, "mid": v(-37.62, -38.53) * mm, "end": v(-37.43, -38.35) * mm});
            skLineSegment(sketch, "E337", {"start": v(-37.87, -38.6) * mm, "end": v(-39.5, -38.6) * mm});
            skArc(sketch, "E338", {"start": v(-40, -38.1) * mm, "mid": v(-39.85, -38.45) * mm, "end": v(-39.5, -38.6) * mm});
            skLineSegment(sketch, "E339", {"start": v(-40, -38.1) * mm, "end": v(-40, -33.1) * mm});
            skArc(sketch, "E340", {"start": v(-39.5, -32.6) * mm, "mid": v(-39.85, -32.75) * mm, "end": v(-40, -33.1) * mm});
            skLineSegment(sketch, "E341", {"start": v(-39.5, -32.6) * mm, "end": v(-37.87, -32.6) * mm});
            skArc(sketch, "E342", {"start": v(-37.43, -32.85) * mm, "mid": v(-37.62, -32.67) * mm, "end": v(-37.87, -32.6) * mm});
            skArc(sketch, "E343", {"start": v(-37.43, -32.85) * mm, "mid": v(-36.65, -32.95) * mm, "end": v(-36.75, -32.17) * mm});
            skArc(sketch, "E344", {"start": v(-37, -31.73) * mm, "mid": v(-36.93, -31.98) * mm, "end": v(-36.75, -32.17) * mm});
            skLineSegment(sketch, "E345", {"start": v(-37, -31.73) * mm, "end": v(-37, -26.6) * mm});
            skLineSegment(sketch, "E346", {"start": v(-37, -26.6) * mm, "end": v(-34, -26.6) * mm});
            skLineSegment(sketch, "E347", {"start": v(-34, -26.6) * mm, "end": v(-34, -27.88) * mm});
            skLineSegment(sketch, "E348", {"start": v(-34, -27.88) * mm, "end": v(-30, -27.88) * mm});
            skLineSegment(sketch, "E349", {"start": v(-30, -27.88) * mm, "end": v(-30, -26.6) * mm});
            skLineSegment(sketch, "E350", {"start": v(-30, -26.6) * mm, "end": v(-27, -26.6) * mm});
            skLineSegment(sketch, "E351", {"start": v(-27, -26.6) * mm, "end": v(-27, -23.4) * mm});
            skLineSegment(sketch, "E352", {"start": v(-27, -23.4) * mm, "end": v(-30, -23.4) * mm});
            skLineSegment(sketch, "E353", {"start": v(-30, -23.4) * mm, "end": v(-30, -22.13) * mm});
            skLineSegment(sketch, "E354", {"start": v(-30, -22.13) * mm, "end": v(-34, -22.13) * mm});
            skLineSegment(sketch, "E355", {"start": v(-34, -22.13) * mm, "end": v(-34, -23.4) * mm});
            skLineSegment(sketch, "E356", {"start": v(-34, -23.4) * mm, "end": v(-37, -23.4) * mm});
            skLineSegment(sketch, "E357", {"start": v(-37, -23.4) * mm, "end": v(-37, -18.27) * mm});
            skArc(sketch, "E358", {"start": v(-36.75, -17.83) * mm, "mid": v(-36.93, -18.02) * mm, "end": v(-37, -18.27) * mm});
            skArc(sketch, "E359", {"start": v(-36.75, -17.83) * mm, "mid": v(-36.65, -17.05) * mm, "end": v(-37.43, -17.15) * mm});
            skArc(sketch, "E360", {"start": v(-37.87, -17.4) * mm, "mid": v(-37.62, -17.33) * mm, "end": v(-37.43, -17.15) * mm});
            skLineSegment(sketch, "E361", {"start": v(-37.87, -17.4) * mm, "end": v(-39.5, -17.4) * mm});
            skArc(sketch, "E362", {"start": v(-40, -16.9) * mm, "mid": v(-39.85, -17.25) * mm, "end": v(-39.5, -17.4) * mm});
            skLineSegment(sketch, "E363", {"start": v(-40, -16.9) * mm, "end": v(-40, -11.9) * mm});
            skArc(sketch, "E364", {"start": v(-39.5, -11.4) * mm, "mid": v(-39.85, -11.55) * mm, "end": v(-40, -11.9) * mm});
            skLineSegment(sketch, "E365", {"start": v(-39.5, -11.4) * mm, "end": v(-37.87, -11.4) * mm});
            skArc(sketch, "E366", {"start": v(-37.43, -11.65) * mm, "mid": v(-37.62, -11.47) * mm, "end": v(-37.87, -11.4) * mm});
            skArc(sketch, "E367", {"start": v(-37.43, -11.65) * mm, "mid": v(-36.65, -11.75) * mm, "end": v(-36.75, -10.97) * mm});
            skArc(sketch, "E368", {"start": v(-37, -10.53) * mm, "mid": v(-36.93, -10.78) * mm, "end": v(-36.75, -10.97) * mm});
            skLineSegment(sketch, "E369", {"start": v(-37, -10.53) * mm, "end": v(-37, 0) * mm});
            skLineSegment(sketch, "E370", {"start": v(-37, 0) * mm, "end": v(-26.35, 0) * mm});
            skLineSegment(sketch, "E371", {"start": v(-26.35, 0) * mm, "end": v(-26.35, -2.23) * mm});
            skArc(sketch, "E372", {"start": v(-26.6, -2.67) * mm, "mid": v(-26.42, -2.48) * mm, "end": v(-26.35, -2.23) * mm});
            skArc(sketch, "E373", {"start": v(-26.6, -2.67) * mm, "mid": v(-26.7, -3.45) * mm, "end": v(-25.92, -3.35) * mm});
            skArc(sketch, "E374", {"start": v(-25.48, -3.1) * mm, "mid": v(-25.73, -3.17) * mm, "end": v(-25.92, -3.35) * mm});
            skLineSegment(sketch, "E375", {"start": v(-25.48, -3.1) * mm, "end": v(-17.95, -3.1) * mm});
            skLineSegment(sketch, "E376", {"start": v(-17.95, -3.1) * mm, "end": v(-17.95, -6.1) * mm});
            skLineSegment(sketch, "E377", {"start": v(-17.95, -6.1) * mm, "end": v(-19.22, -6.1) * mm});
            skLineSegment(sketch, "E378", {"start": v(-19.22, -6.1) * mm, "end": v(-19.22, -10.1) * mm});
            skLineSegment(sketch, "E379", {"start": v(-19.22, -10.1) * mm, "end": v(-17.95, -10.1) * mm});
            skLineSegment(sketch, "E380", {"start": v(-17.95, -10.1) * mm, "end": v(-17.95, -13.1) * mm});
            skLineSegment(sketch, "E381", {"start": v(-17.95, -13.1) * mm, "end": v(-14.75, -13.1) * mm});
            skLineSegment(sketch, "E382", {"start": v(-14.75, -13.1) * mm, "end": v(-14.75, -10.1) * mm});
            skLineSegment(sketch, "E383", {"start": v(-14.75, -10.1) * mm, "end": v(-13.47, -10.1) * mm});
            skLineSegment(sketch, "E384", {"start": v(-13.47, -10.1) * mm, "end": v(-13.47, -6.1) * mm});
            skLineSegment(sketch, "E385", {"start": v(-13.47, -6.1) * mm, "end": v(-14.75, -6.1) * mm});
            skLineSegment(sketch, "E386", {"start": v(-14.75, -6.1) * mm, "end": v(-14.75, -3.1) * mm});
            skLineSegment(sketch, "E387", {"start": v(-35, -161.5) * mm, "end": v(-35, -158.5) * mm});
            skLineSegment(sketch, "E388", {"start": v(-35, -209.5) * mm, "end": v(-35, -206.5) * mm});
            skLineSegment(sketch, "E389", {"start": v(-35, -285.5) * mm, "end": v(-35, -282.5) * mm});
            skLineSegment(sketch, "E390", {"start": v(-35, -106.5) * mm, "end": v(-35, -103.5) * mm});
            skCircle(sketch, "E391", {"center": v(-30, -160) * mm, "radius": 1.55 * mm});
            skCircle(sketch, "E392", {"center": v(-30, -208) * mm, "radius": 1.55 * mm});
            skCircle(sketch, "E393", {"center": v(-30, -284) * mm, "radius": 1.55 * mm});
            skCircle(sketch, "E394", {"center": v(-30, -105) * mm, "radius": 1.55 * mm});
            skLineSegment(sketch, "E395", {"start": v(-35, -49) * mm, "end": v(-35, -46) * mm});
            skArc(sketch, "E396", {"start": v(-26, -33) * mm, "mid": v(-30, -37) * mm, "end": v(-26, -41) * mm});
            skArc(sketch, "E397", {"start": v(-6, -41) * mm, "mid": v(-2, -37) * mm, "end": v(-6, -33) * mm});
            skLineSegment(sketch, "E398", {"start": v(-26, -41) * mm, "end": v(-6, -41) * mm});
            skLineSegment(sketch, "E399", {"start": v(-6, -33) * mm, "end": v(-26, -33) * mm});
            skCircle(sketch, "E400", {"center": v(26, -312) * mm, "radius": 1.55 * mm});
            skCircle(sketch, "E401", {"center": v(36, -312) * mm, "radius": 1.55 * mm});
            skCircle(sketch, "E402", {"center": v(56, -312) * mm, "radius": 1.55 * mm});
            skCircle(sketch, "E403", {"center": v(66, -312) * mm, "radius": 1.55 * mm});
            skCircle(sketch, "E404", {"center": v(-4, -312) * mm, "radius": 1.55 * mm});
            skCircle(sketch, "E405", {"center": v(6, -312) * mm, "radius": 1.55 * mm});
            skLineSegment(sketch, "E406", {"start": v(-37, -290.53) * mm, "end": v(-37, -286) * mm});
            skLineSegment(sketch, "E407", {"start": v(-36.5, -285.5) * mm, "end": v(-35, -285.5) * mm});
            skLineSegment(sketch, "E408", {"start": v(-37, -286) * mm, "end": v(-36.5, -285.5) * mm});
            skLineSegment(sketch, "E409", {"start": v(-35, -282.5) * mm, "end": v(-36.5, -282.5) * mm});
            skLineSegment(sketch, "E410", {"start": v(-37, -282) * mm, "end": v(-36.5, -282.5) * mm});
            skLineSegment(sketch, "E411", {"start": v(-37, -282) * mm, "end": v(-37, -210) * mm});
            skLineSegment(sketch, "E412", {"start": v(-36.5, -209.5) * mm, "end": v(-35, -209.5) * mm});
            skLineSegment(sketch, "E413", {"start": v(-37, -210) * mm, "end": v(-36.5, -209.5) * mm});
            skLineSegment(sketch, "E414", {"start": v(-37, -206) * mm, "end": v(-37, -199.47) * mm});
            skLineSegment(sketch, "E415", {"start": v(-35, -206.5) * mm, "end": v(-36.5, -206.5) * mm});
            skLineSegment(sketch, "E416", {"start": v(-37, -206) * mm, "end": v(-36.5, -206.5) * mm});
            skLineSegment(sketch, "E417", {"start": v(-37, -170.53) * mm, "end": v(-37, -162) * mm});
            skLineSegment(sketch, "E418", {"start": v(-36.5, -161.5) * mm, "end": v(-35, -161.5) * mm});
            skLineSegment(sketch, "E419", {"start": v(-37, -162) * mm, "end": v(-36.5, -161.5) * mm});
            skLineSegment(sketch, "E420", {"start": v(-35, -158.5) * mm, "end": v(-36.5, -158.5) * mm});
            skLineSegment(sketch, "E421", {"start": v(-37, -158) * mm, "end": v(-36.5, -158.5) * mm});
            skLineSegment(sketch, "E422", {"start": v(-37, -158) * mm, "end": v(-37, -107) * mm});
            skLineSegment(sketch, "E423", {"start": v(-36.5, -106.5) * mm, "end": v(-35, -106.5) * mm});
            skLineSegment(sketch, "E424", {"start": v(-37, -107) * mm, "end": v(-36.5, -106.5) * mm});
            skLineSegment(sketch, "E425", {"start": v(-35, -103.5) * mm, "end": v(-36.5, -103.5) * mm});
            skLineSegment(sketch, "E426", {"start": v(-37, -103) * mm, "end": v(-36.5, -103.5) * mm});
            skLineSegment(sketch, "E427", {"start": v(-37, -103) * mm, "end": v(-37, -49.5) * mm});
            skLineSegment(sketch, "E428", {"start": v(-36.5, -49) * mm, "end": v(-35, -49) * mm});
            skLineSegment(sketch, "E429", {"start": v(-37, -49.5) * mm, "end": v(-36.5, -49) * mm});
            skLineSegment(sketch, "E430", {"start": v(-37, -45.5) * mm, "end": v(-37, -39.47) * mm});
            skLineSegment(sketch, "E431", {"start": v(-35, -46) * mm, "end": v(-36.5, -46) * mm});
            skLineSegment(sketch, "E432", {"start": v(-37, -45.5) * mm, "end": v(-36.5, -46) * mm});
            skArc(sketch, "E433", {"start": v(92.75, -330.97) * mm, "mid": v(92.93, -330.78) * mm, "end": v(93, -330.53) * mm});
            skArc(sketch, "E434", {"start": v(92.75, -330.97) * mm, "mid": v(92.65, -331.75) * mm, "end": v(93.43, -331.65) * mm});
            skArc(sketch, "E435", {"start": v(93.87, -331.4) * mm, "mid": v(93.62, -331.47) * mm, "end": v(93.43, -331.65) * mm});
            skLineSegment(sketch, "E436", {"start": v(93.87, -331.4) * mm, "end": v(95.5, -331.4) * mm});
            skArc(sketch, "E437", {"start": v(96, -331.9) * mm, "mid": v(95.85, -331.55) * mm, "end": v(95.5, -331.4) * mm});
            skLineSegment(sketch, "E438", {"start": v(96, -331.9) * mm, "end": v(96, -336.9) * mm});
            skArc(sketch, "E439", {"start": v(95.5, -337.4) * mm, "mid": v(95.85, -337.25) * mm, "end": v(96, -336.9) * mm});
            skLineSegment(sketch, "E440", {"start": v(95.5, -337.4) * mm, "end": v(93.87, -337.4) * mm});
            skArc(sketch, "E441", {"start": v(93.43, -337.15) * mm, "mid": v(93.62, -337.33) * mm, "end": v(93.87, -337.4) * mm});
            skArc(sketch, "E442", {"start": v(93.43, -337.15) * mm, "mid": v(92.65, -337.05) * mm, "end": v(92.75, -337.83) * mm});
            skArc(sketch, "E443", {"start": v(93, -338.27) * mm, "mid": v(92.93, -338.02) * mm, "end": v(92.75, -337.83) * mm});
            skLineSegment(sketch, "E444", {"start": v(93, -338.27) * mm, "end": v(93, -343.4) * mm});
            skLineSegment(sketch, "E445", {"start": v(93, -343.4) * mm, "end": v(90, -343.4) * mm});
            skLineSegment(sketch, "E446", {"start": v(90, -343.4) * mm, "end": v(90, -342.13) * mm});
            skLineSegment(sketch, "E447", {"start": v(90, -342.13) * mm, "end": v(86, -342.13) * mm});
            skLineSegment(sketch, "E448", {"start": v(86, -342.13) * mm, "end": v(86, -343.4) * mm});
            skLineSegment(sketch, "E449", {"start": v(86, -343.4) * mm, "end": v(83, -343.4) * mm});
            skLineSegment(sketch, "E450", {"start": v(83, -343.4) * mm, "end": v(83, -346.6) * mm});
            skLineSegment(sketch, "E451", {"start": v(83, -346.6) * mm, "end": v(86, -346.6) * mm});
            skLineSegment(sketch, "E452", {"start": v(86, -346.6) * mm, "end": v(86, -347.88) * mm});
            skLineSegment(sketch, "E453", {"start": v(86, -347.88) * mm, "end": v(90, -347.88) * mm});
            skLineSegment(sketch, "E454", {"start": v(90, -347.88) * mm, "end": v(90, -346.6) * mm});
            skLineSegment(sketch, "E455", {"start": v(90, -346.6) * mm, "end": v(93, -346.6) * mm});
            skLineSegment(sketch, "E456", {"start": v(93, -346.6) * mm, "end": v(93, -351.73) * mm});
            skArc(sketch, "E457", {"start": v(92.75, -352.17) * mm, "mid": v(92.93, -351.98) * mm, "end": v(93, -351.73) * mm});
            skArc(sketch, "E458", {"start": v(92.75, -352.17) * mm, "mid": v(92.65, -352.95) * mm, "end": v(93.43, -352.85) * mm});
            skArc(sketch, "E459", {"start": v(93.87, -352.6) * mm, "mid": v(93.62, -352.67) * mm, "end": v(93.43, -352.85) * mm});
            skLineSegment(sketch, "E460", {"start": v(93.87, -352.6) * mm, "end": v(95.5, -352.6) * mm});
            skArc(sketch, "E461", {"start": v(96, -353.1) * mm, "mid": v(95.85, -352.75) * mm, "end": v(95.5, -352.6) * mm});
            skLineSegment(sketch, "E462", {"start": v(96, -353.1) * mm, "end": v(96, -358.1) * mm});
            skArc(sketch, "E463", {"start": v(95.5, -358.6) * mm, "mid": v(95.85, -358.45) * mm, "end": v(96, -358.1) * mm});
            skLineSegment(sketch, "E464", {"start": v(95.5, -358.6) * mm, "end": v(93.87, -358.6) * mm});
            skArc(sketch, "E465", {"start": v(93.43, -358.35) * mm, "mid": v(93.62, -358.53) * mm, "end": v(93.87, -358.6) * mm});
            skArc(sketch, "E466", {"start": v(93.43, -358.35) * mm, "mid": v(92.65, -358.25) * mm, "end": v(92.75, -359.03) * mm});
            skArc(sketch, "E467", {"start": v(93, -359.47) * mm, "mid": v(92.93, -359.22) * mm, "end": v(92.75, -359.03) * mm});
            skLineSegment(sketch, "E468", {"start": v(93, -359.47) * mm, "end": v(93, -370) * mm});
            skLineSegment(sketch, "E469", {"start": v(93, -325.55) * mm, "end": v(93, -330.53) * mm});
            skLineSegment(sketch, "E470", {"start": v(82.35, 0) * mm, "end": v(82.35, -2.23) * mm});
            skArc(sketch, "E471", {"start": v(81.92, -3.35) * mm, "mid": v(82.7, -3.45) * mm, "end": v(82.6, -2.67) * mm});
            skLineSegment(sketch, "E472", {"start": v(93, -370) * mm, "end": v(72.83, -370) * mm});
            skArc(sketch, "E473", {"start": v(71.41, -369.41) * mm, "mid": v(72.06, -369.85) * mm, "end": v(72.83, -370) * mm});
            skLineSegment(sketch, "E474", {"start": v(71.41, -369.41) * mm, "end": v(70.59, -368.59) * mm});
            skArc(sketch, "E475", {"start": v(70.59, -368.59) * mm, "mid": v(69.94, -368.15) * mm, "end": v(69.17, -368) * mm});
            skLineSegment(sketch, "E476", {"start": v(93, 0) * mm, "end": v(82.35, 0) * mm});
            skLineSegment(sketch, "E477", {"start": v(73.95, -6.1) * mm, "end": v(75.23, -6.1) * mm});
            skLineSegment(sketch, "E478", {"start": v(75.23, -6.1) * mm, "end": v(75.23, -10.1) * mm});
            skLineSegment(sketch, "E479", {"start": v(75.23, -10.1) * mm, "end": v(73.95, -10.1) * mm});
            skLineSegment(sketch, "E480", {"start": v(73.95, -10.1) * mm, "end": v(73.95, -13.1) * mm});
            skLineSegment(sketch, "E481", {"start": v(73.95, -13.1) * mm, "end": v(70.75, -13.1) * mm});
            skLineSegment(sketch, "E482", {"start": v(70.75, -13.1) * mm, "end": v(70.75, -10.1) * mm});
            skLineSegment(sketch, "E483", {"start": v(70.75, -10.1) * mm, "end": v(69.48, -10.1) * mm});
            skLineSegment(sketch, "E484", {"start": v(69.48, -10.1) * mm, "end": v(69.48, -6.1) * mm});
            skLineSegment(sketch, "E485", {"start": v(69.48, -6.1) * mm, "end": v(70.75, -6.1) * mm});
            skLineSegment(sketch, "E486", {"start": v(81.48, -3.1) * mm, "end": v(73.95, -3.1) * mm});
            skLineSegment(sketch, "E487", {"start": v(70.75, -6.1) * mm, "end": v(70.75, -3.1) * mm});
            skLineSegment(sketch, "E488", {"start": v(-14.75, -3.1) * mm, "end": v(70.75, -3.1) * mm});
            skLineSegment(sketch, "E489", {"start": v(69.17, -368) * mm, "end": v(-37, -368) * mm});
            skArc(sketch, "E490", {"start": v(53.8, -147) * mm, "mid": v(56, -149.2) * mm, "end": v(58.2, -147) * mm});
            skArc(sketch, "E491", {"start": v(3.8, -147) * mm, "mid": v(6, -149.2) * mm, "end": v(8.2, -147) * mm});
            skArc(sketch, "E492", {"start": v(63, -166) * mm, "mid": v(64.17, -168.83) * mm, "end": v(67, -170) * mm});
            skLineSegment(sketch, "E493", {"start": v(79, -170) * mm, "end": v(67, -170) * mm});
            skArc(sketch, "E494", {"start": v(79, -170) * mm, "mid": v(81.83, -168.83) * mm, "end": v(83, -166) * mm});
            skArc(sketch, "E495", {"start": v(67, -184) * mm, "mid": v(64.17, -185.17) * mm, "end": v(63, -188) * mm});
            skLineSegment(sketch, "E496", {"start": v(79, -184) * mm, "end": v(67, -184) * mm});
            skArc(sketch, "E497", {"start": v(83, -188) * mm, "mid": v(81.83, -185.17) * mm, "end": v(79, -184) * mm});
            skArc(sketch, "E498", {"start": v(-5, -170) * mm, "mid": v(-2.17, -168.83) * mm, "end": v(-1, -166) * mm});
            skLineSegment(sketch, "E499", {"start": v(-17, -170) * mm, "end": v(-5, -170) * mm});
            skArc(sketch, "E500", {"start": v(-21, -166) * mm, "mid": v(-19.83, -168.83) * mm, "end": v(-17, -170) * mm});
            skArc(sketch, "E501", {"start": v(-1, -188) * mm, "mid": v(-2.17, -185.17) * mm, "end": v(-5, -184) * mm});
            skLineSegment(sketch, "E502", {"start": v(-17, -184) * mm, "end": v(-5, -184) * mm});
            skArc(sketch, "E503", {"start": v(-17, -184) * mm, "mid": v(-19.83, -185.17) * mm, "end": v(-21, -188) * mm});
            skArc(sketch, "E504", {"start": v(45, -170) * mm, "mid": v(47.83, -168.83) * mm, "end": v(49, -166) * mm});
            skArc(sketch, "E505", {"start": v(13, -166) * mm, "mid": v(14.17, -168.83) * mm, "end": v(17, -170) * mm});
            skLineSegment(sketch, "E506", {"start": v(17, -170) * mm, "end": v(45, -170) * mm});
            skArc(sketch, "E507", {"start": v(49, -188) * mm, "mid": v(47.83, -185.17) * mm, "end": v(45, -184) * mm});
            skArc(sketch, "E508", {"start": v(17, -184) * mm, "mid": v(14.17, -185.17) * mm, "end": v(13, -188) * mm});
            skLineSegment(sketch, "E509", {"start": v(17, -184) * mm, "end": v(45, -184) * mm});
            skArc(sketch, "E510", {"start": v(-1, -74) * mm, "mid": v(-2.17, -71.17) * mm, "end": v(-5, -70) * mm});
            skLineSegment(sketch, "E511", {"start": v(-5, -70) * mm, "end": v(-17, -70) * mm});
            skArc(sketch, "E512", {"start": v(-17, -70) * mm, "mid": v(-19.83, -71.17) * mm, "end": v(-21, -74) * mm});
            skLineSegment(sketch, "E513", {"start": v(-1, -166) * mm, "end": v(-1, -74) * mm});
            skLineSegment(sketch, "E514", {"start": v(-21, -74) * mm, "end": v(-21, -166) * mm});
            skArc(sketch, "E515", {"start": v(49, -74) * mm, "mid": v(47.83, -71.17) * mm, "end": v(45, -70) * mm});
            skLineSegment(sketch, "E516", {"start": v(49, -166) * mm, "end": v(49, -74) * mm});
            skArc(sketch, "E517", {"start": v(17, -70) * mm, "mid": v(14.17, -71.17) * mm, "end": v(13, -74) * mm});
            skLineSegment(sketch, "E518", {"start": v(13, -166) * mm, "end": v(13, -74) * mm});
            skLineSegment(sketch, "E519", {"start": v(17, -70) * mm, "end": v(45, -70) * mm});
            skArc(sketch, "E520", {"start": v(67, -70) * mm, "mid": v(64.17, -71.17) * mm, "end": v(63, -74) * mm});
            skLineSegment(sketch, "E521", {"start": v(67, -70) * mm, "end": v(79, -70) * mm});
            skArc(sketch, "E522", {"start": v(83, -74) * mm, "mid": v(81.83, -71.17) * mm, "end": v(79, -70) * mm});
            skLineSegment(sketch, "E523", {"start": v(63, -166) * mm, "end": v(63, -74) * mm});
            skLineSegment(sketch, "E524", {"start": v(83, -74) * mm, "end": v(83, -166) * mm});
            skArc(sketch, "E525", {"start": v(-5, -284) * mm, "mid": v(-2.17, -282.83) * mm, "end": v(-1, -280) * mm});
            skLineSegment(sketch, "E526", {"start": v(-5, -284) * mm, "end": v(-17, -284) * mm});
            skArc(sketch, "E527", {"start": v(-21, -280) * mm, "mid": v(-19.83, -282.83) * mm, "end": v(-17, -284) * mm});
            skLineSegment(sketch, "E528", {"start": v(-1, -188) * mm, "end": v(-1, -280) * mm});
            skLineSegment(sketch, "E529", {"start": v(-21, -280) * mm, "end": v(-21, -188) * mm});
            skArc(sketch, "E530", {"start": v(45, -284) * mm, "mid": v(47.83, -282.83) * mm, "end": v(49, -280) * mm});
            skLineSegment(sketch, "E531", {"start": v(49, -188) * mm, "end": v(49, -280) * mm});
            skArc(sketch, "E532", {"start": v(13, -280) * mm, "mid": v(14.17, -282.83) * mm, "end": v(17, -284) * mm});
            skLineSegment(sketch, "E533", {"start": v(13, -188) * mm, "end": v(13, -280) * mm});
            skLineSegment(sketch, "E534", {"start": v(17, -284) * mm, "end": v(45, -284) * mm});
            skArc(sketch, "E535", {"start": v(63, -280) * mm, "mid": v(64.17, -282.83) * mm, "end": v(67, -284) * mm});
            skLineSegment(sketch, "E536", {"start": v(67, -284) * mm, "end": v(79, -284) * mm});
            skArc(sketch, "E537", {"start": v(79, -284) * mm, "mid": v(81.83, -282.83) * mm, "end": v(83, -280) * mm});
            skLineSegment(sketch, "E538", {"start": v(63, -188) * mm, "end": v(63, -280) * mm});
            skLineSegment(sketch, "E539", {"start": v(83, -280) * mm, "end": v(83, -188) * mm});
            skCircle(sketch, "E540", {"center": v(-27, -47) * mm, "radius": 1.55 * mm});
            skCircle(sketch, "E541", {"center": v(-17, -47) * mm, "radius": 1.55 * mm});
            skCircle(sketch, "E542", {"center": v(-4, -47) * mm, "radius": 1.55 * mm});
            skCircle(sketch, "E543", {"center": v(6, -47) * mm, "radius": 1.55 * mm});
            skCircle(sketch, "E544", {"center": v(26, -47) * mm, "radius": 1.55 * mm});
            skCircle(sketch, "E545", {"center": v(36, -47) * mm, "radius": 1.55 * mm});
            skCircle(sketch, "E546", {"center": v(56, -47) * mm, "radius": 1.55 * mm});
            skCircle(sketch, "E547", {"center": v(66, -47) * mm, "radius": 1.55 * mm});
            skCircle(sketch, "E548", {"center": v(78, -47) * mm, "radius": 1.55 * mm});
            skArc(sketch, "E549", {"start": v(8.2, -67) * mm, "mid": v(6, -64.8) * mm, "end": v(3.8, -67) * mm});
            skLineSegment(sketch, "E550", {"start": v(8.2, -67) * mm, "end": v(8.2, -147) * mm});
            skLineSegment(sketch, "E551", {"start": v(3.8, -67) * mm, "end": v(3.8, -147) * mm});
            skArc(sketch, "E552", {"start": v(58.2, -67) * mm, "mid": v(56, -64.8) * mm, "end": v(53.8, -67) * mm});
            skLineSegment(sketch, "E553", {"start": v(58.2, -67) * mm, "end": v(58.2, -147) * mm});
            skLineSegment(sketch, "E554", {"start": v(53.8, -67) * mm, "end": v(53.8, -147) * mm});
            skArc(sketch, "E555", {"start": v(58.2, -207) * mm, "mid": v(56, -204.8) * mm, "end": v(53.8, -207) * mm});
            skArc(sketch, "E556", {"start": v(8.2, -207) * mm, "mid": v(6, -204.8) * mm, "end": v(3.8, -207) * mm});
            skArc(sketch, "E557", {"start": v(3.8, -287) * mm, "mid": v(6, -289.2) * mm, "end": v(8.2, -287) * mm});
            skLineSegment(sketch, "E558", {"start": v(8.2, -287) * mm, "end": v(8.2, -207) * mm});
            skLineSegment(sketch, "E559", {"start": v(3.8, -287) * mm, "end": v(3.8, -207) * mm});
            skArc(sketch, "E560", {"start": v(53.8, -287) * mm, "mid": v(56, -289.2) * mm, "end": v(58.2, -287) * mm});
            skLineSegment(sketch, "E561", {"start": v(58.2, -287) * mm, "end": v(58.2, -207) * mm});
            skLineSegment(sketch, "E562", {"start": v(53.8, -287) * mm, "end": v(53.8, -207) * mm});
            skArc(sketch, "E563", {"start": v(83, -31.5) * mm, "mid": v(81.4, -33.1) * mm, "end": v(83, -34.7) * mm});
            skLineSegment(sketch, "E564", {"start": v(83, -31.5) * mm, "end": v(92.75, -31.5) * mm});
            skLineSegment(sketch, "E565", {"start": v(93, -31.25) * mm, "end": v(93, 0) * mm});
            skLineSegment(sketch, "E566", {"start": v(92.75, -31.5) * mm, "end": v(93, -31.25) * mm});
            skLineSegment(sketch, "E567", {"start": v(83, -34.7) * mm, "end": v(92.75, -34.7) * mm});
            skLineSegment(sketch, "E568", {"start": v(93, -325.55) * mm, "end": v(93, -34.95) * mm});
            skLineSegment(sketch, "E569", {"start": v(92.75, -34.7) * mm, "end": v(93, -34.95) * mm});
            skLineSegment(sketch, "E570", {"start": v(-46.55, -331.4) * mm, "end": v(-46.55, -358.6) * mm});
            skLineSegment(sketch, "E571", {"start": v(-37.87, -331.4) * mm, "end": v(-46.55, -331.4) * mm});
            skLineSegment(sketch, "E572", {"start": v(-37.87, -358.6) * mm, "end": v(-46.55, -358.6) * mm});
            skPoint(sketch, "E573.start.orphan", {"position": v(-40, -174.4) * mm});
            skPoint(sketch, "E574.orphan", {"position": v(77.72, -3.1) * mm});
            skArc(sketch, "E575", {"start": v(81.48, -3.1) * mm, "mid": v(81.73, -3.17) * mm, "end": v(81.92, -3.35) * mm});
            skArc(sketch, "E576", {"start": v(82.6, -2.67) * mm, "mid": v(82.38, -2.41) * mm, "end": v(82.35, -2.08) * mm});
            skLineSegment(sketch, "E577", {"start": v(73.95, -3.1) * mm, "end": v(73.95, -6.1) * mm});
            skSolve(sketch);
        }
        {
            var Q0;
            {var subQ0=sQuery(id+"F7.wireOp",EDGE,"E256");Q0=makeQuery(id+"F7.imprint","IMPRINT",FACE,{"disambiguationData":[TD([[makeQuery(id+"F7.imprint","IMPRINT",EDGE,{"derivedFrom":subQ0}),-1.0]])]});}
            extrude(context, id + "F8", {"entities" : qUnion([Q0]), "depth" : 3 * mm, "offsetDistance" : 25 * mm});
        }
        {
            var Q0;
            Q0=makeQuery(id+"F8.opExtrude","CAP_FACE",FACE,{"disambiguationData":[OSD([sQuery(id+"F7.wireOp",EDGE,"E256"),sQuery(id+"F7.wireOp",EDGE,"E257"),sQuery(id+"F7.wireOp",EDGE,"E258"),sQuery(id+"F7.wireOp",EDGE,"E259"),sQuery(id+"F7.wireOp",EDGE,"E260"),sQuery(id+"F7.wireOp",EDGE,"E261"),sQuery(id+"F7.wireOp",EDGE,"E262"),sQuery(id+"F7.wireOp",EDGE,"E263"),sQuery(id+"F7.wireOp",EDGE,"E264"),sQuery(id+"F7.wireOp",EDGE,"E265"),sQuery(id+"F7.wireOp",EDGE,"E266"),sQuery(id+"F7.wireOp",EDGE,"E267"),sQuery(id+"F7.wireOp",EDGE,"E268"),sQuery(id+"F7.wireOp",EDGE,"E269"),sQuery(id+"F7.wireOp",EDGE,"E270"),sQuery(id+"F7.wireOp",EDGE,"E271"),sQuery(id+"F7.wireOp",EDGE,"E272"),sQuery(id+"F7.wireOp",EDGE,"E273"),sQuery(id+"F7.wireOp",EDGE,"E274"),sQuery(id+"F7.wireOp",EDGE,"E275"),sQuery(id+"F7.wireOp",EDGE,"E276"),sQuery(id+"F7.wireOp",EDGE,"E277"),sQuery(id+"F7.wireOp",EDGE,"E278"),sQuery(id+"F7.wireOp",EDGE,"E279"),sQuery(id+"F7.wireOp",EDGE,"E280"),sQuery(id+"F7.wireOp",EDGE,"E281"),sQuery(id+"F7.wireOp",EDGE,"E282"),sQuery(id+"F7.wireOp",EDGE,"E283"),sQuery(id+"F7.wireOp",EDGE,"E284"),sQuery(id+"F7.wireOp",EDGE,"E285"),sQuery(id+"F7.wireOp",EDGE,"E286"),sQuery(id+"F7.wireOp",EDGE,"E287"),sQuery(id+"F7.wireOp",EDGE,"E288"),sQuery(id+"F7.wireOp",EDGE,"E289"),sQuery(id+"F7.wireOp",EDGE,"E290"),sQuery(id+"F7.wireOp",EDGE,"E291"),sQuery(id+"F7.wireOp",EDGE,"E292"),sQuery(id+"F7.wireOp",EDGE,"E293"),sQuery(id+"F7.wireOp",EDGE,"E294"),sQuery(id+"F7.wireOp",EDGE,"E295"),sQuery(id+"F7.wireOp",EDGE,"E296"),sQuery(id+"F7.wireOp",EDGE,"E297"),sQuery(id+"F7.wireOp",EDGE,"E298"),sQuery(id+"F7.wireOp",EDGE,"E299"),sQuery(id+"F7.wireOp",EDGE,"E300"),sQuery(id+"F7.wireOp",EDGE,"E301"),sQuery(id+"F7.wireOp",EDGE,"E302"),sQuery(id+"F7.wireOp",EDGE,"E303"),sQuery(id+"F7.wireOp",EDGE,"E304"),sQuery(id+"F7.wireOp",EDGE,"E305"),sQuery(id+"F7.wireOp",EDGE,"E306"),sQuery(id+"F7.wireOp",EDGE,"E307"),sQuery(id+"F7.wireOp",EDGE,"E308"),sQuery(id+"F7.wireOp",EDGE,"E309"),sQuery(id+"F7.wireOp",EDGE,"E310"),sQuery(id+"F7.wireOp",EDGE,"E311"),sQuery(id+"F7.wireOp",EDGE,"E312"),sQuery(id+"F7.wireOp",EDGE,"E313"),sQuery(id+"F7.wireOp",EDGE,"E314"),sQuery(id+"F7.wireOp",EDGE,"E315"),sQuery(id+"F7.wireOp",EDGE,"E316"),sQuery(id+"F7.wireOp",EDGE,"E317"),sQuery(id+"F7.wireOp",EDGE,"E318"),sQuery(id+"F7.wireOp",EDGE,"E319"),sQuery(id+"F7.wireOp",EDGE,"E320"),sQuery(id+"F7.wireOp",EDGE,"E321"),sQuery(id+"F7.wireOp",EDGE,"E322"),sQuery(id+"F7.wireOp",EDGE,"E323"),sQuery(id+"F7.wireOp",EDGE,"E324"),sQuery(id+"F7.wireOp",EDGE,"E325"),sQuery(id+"F7.wireOp",EDGE,"E326"),sQuery(id+"F7.wireOp",EDGE,"E327"),sQuery(id+"F7.wireOp",EDGE,"E328"),sQuery(id+"F7.wireOp",EDGE,"E329"),sQuery(id+"F7.wireOp",EDGE,"E330"),sQuery(id+"F7.wireOp",EDGE,"E331"),sQuery(id+"F7.wireOp",EDGE,"E332"),sQuery(id+"F7.wireOp",EDGE,"E333"),sQuery(id+"F7.wireOp",EDGE,"E334"),sQuery(id+"F7.wireOp",EDGE,"E335"),sQuery(id+"F7.wireOp",EDGE,"E336"),sQuery(id+"F7.wireOp",EDGE,"E337"),sQuery(id+"F7.wireOp",EDGE,"E338"),sQuery(id+"F7.wireOp",EDGE,"E339"),sQuery(id+"F7.wireOp",EDGE,"E340"),sQuery(id+"F7.wireOp",EDGE,"E341"),sQuery(id+"F7.wireOp",EDGE,"E342"),sQuery(id+"F7.wireOp",EDGE,"E343"),sQuery(id+"F7.wireOp",EDGE,"E344"),sQuery(id+"F7.wireOp",EDGE,"E345"),sQuery(id+"F7.wireOp",EDGE,"E346"),sQuery(id+"F7.wireOp",EDGE,"E347"),sQuery(id+"F7.wireOp",EDGE,"E348"),sQuery(id+"F7.wireOp",EDGE,"E349"),sQuery(id+"F7.wireOp",EDGE,"E350"),sQuery(id+"F7.wireOp",EDGE,"E351"),sQuery(id+"F7.wireOp",EDGE,"E352"),sQuery(id+"F7.wireOp",EDGE,"E353"),sQuery(id+"F7.wireOp",EDGE,"E354"),sQuery(id+"F7.wireOp",EDGE,"E355"),sQuery(id+"F7.wireOp",EDGE,"E356"),sQuery(id+"F7.wireOp",EDGE,"E357"),sQuery(id+"F7.wireOp",EDGE,"E358"),sQuery(id+"F7.wireOp",EDGE,"E359"),sQuery(id+"F7.wireOp",EDGE,"E360"),sQuery(id+"F7.wireOp",EDGE,"E361"),sQuery(id+"F7.wireOp",EDGE,"E362"),sQuery(id+"F7.wireOp",EDGE,"E363"),sQuery(id+"F7.wireOp",EDGE,"E364"),sQuery(id+"F7.wireOp",EDGE,"E365"),sQuery(id+"F7.wireOp",EDGE,"E366"),sQuery(id+"F7.wireOp",EDGE,"E367"),sQuery(id+"F7.wireOp",EDGE,"E368"),sQuery(id+"F7.wireOp",EDGE,"E369"),sQuery(id+"F7.wireOp",EDGE,"E370"),sQuery(id+"F7.wireOp",EDGE,"E371"),sQuery(id+"F7.wireOp",EDGE,"E372"),sQuery(id+"F7.wireOp",EDGE,"E373"),sQuery(id+"F7.wireOp",EDGE,"E374"),sQuery(id+"F7.wireOp",EDGE,"E375"),sQuery(id+"F7.wireOp",EDGE,"E376"),sQuery(id+"F7.wireOp",EDGE,"E377"),sQuery(id+"F7.wireOp",EDGE,"E378"),sQuery(id+"F7.wireOp",EDGE,"E379"),sQuery(id+"F7.wireOp",EDGE,"E380"),sQuery(id+"F7.wireOp",EDGE,"E381"),sQuery(id+"F7.wireOp",EDGE,"E382"),sQuery(id+"F7.wireOp",EDGE,"E383"),sQuery(id+"F7.wireOp",EDGE,"E384"),sQuery(id+"F7.wireOp",EDGE,"E385"),sQuery(id+"F7.wireOp",EDGE,"E386"),sQuery(id+"F7.wireOp",EDGE,"E387"),sQuery(id+"F7.wireOp",EDGE,"E388"),sQuery(id+"F7.wireOp",EDGE,"E389"),sQuery(id+"F7.wireOp",EDGE,"E390"),sQuery(id+"F7.wireOp",EDGE,"E391"),sQuery(id+"F7.wireOp",EDGE,"E392"),sQuery(id+"F7.wireOp",EDGE,"E393"),sQuery(id+"F7.wireOp",EDGE,"E394"),sQuery(id+"F7.wireOp",EDGE,"E395"),sQuery(id+"F7.wireOp",EDGE,"E396"),sQuery(id+"F7.wireOp",EDGE,"E397"),sQuery(id+"F7.wireOp",EDGE,"E398"),sQuery(id+"F7.wireOp",EDGE,"E399"),sQuery(id+"F7.wireOp",EDGE,"E400"),sQuery(id+"F7.wireOp",EDGE,"E401"),sQuery(id+"F7.wireOp",EDGE,"E402"),sQuery(id+"F7.wireOp",EDGE,"E403"),sQuery(id+"F7.wireOp",EDGE,"E404"),sQuery(id+"F7.wireOp",EDGE,"E405"),sQuery(id+"F7.wireOp",EDGE,"E406"),sQuery(id+"F7.wireOp",EDGE,"E407"),sQuery(id+"F7.wireOp",EDGE,"E408"),sQuery(id+"F7.wireOp",EDGE,"E409"),sQuery(id+"F7.wireOp",EDGE,"E410"),sQuery(id+"F7.wireOp",EDGE,"E411"),sQuery(id+"F7.wireOp",EDGE,"E412"),sQuery(id+"F7.wireOp",EDGE,"E413"),sQuery(id+"F7.wireOp",EDGE,"E414"),sQuery(id+"F7.wireOp",EDGE,"E415"),sQuery(id+"F7.wireOp",EDGE,"E416"),sQuery(id+"F7.wireOp",EDGE,"E417"),sQuery(id+"F7.wireOp",EDGE,"E418"),sQuery(id+"F7.wireOp",EDGE,"E419"),sQuery(id+"F7.wireOp",EDGE,"E420"),sQuery(id+"F7.wireOp",EDGE,"E421"),sQuery(id+"F7.wireOp",EDGE,"E422"),sQuery(id+"F7.wireOp",EDGE,"E423"),sQuery(id+"F7.wireOp",EDGE,"E424"),sQuery(id+"F7.wireOp",EDGE,"E425"),sQuery(id+"F7.wireOp",EDGE,"E426"),sQuery(id+"F7.wireOp",EDGE,"E427"),sQuery(id+"F7.wireOp",EDGE,"E428"),sQuery(id+"F7.wireOp",EDGE,"E429"),sQuery(id+"F7.wireOp",EDGE,"E430"),sQuery(id+"F7.wireOp",EDGE,"E431"),sQuery(id+"F7.wireOp",EDGE,"E432"),sQuery(id+"F7.wireOp",EDGE,"E433"),sQuery(id+"F7.wireOp",EDGE,"E434"),sQuery(id+"F7.wireOp",EDGE,"E435"),sQuery(id+"F7.wireOp",EDGE,"E436"),sQuery(id+"F7.wireOp",EDGE,"E437"),sQuery(id+"F7.wireOp",EDGE,"E438"),sQuery(id+"F7.wireOp",EDGE,"E439"),sQuery(id+"F7.wireOp",EDGE,"E440"),sQuery(id+"F7.wireOp",EDGE,"E441"),sQuery(id+"F7.wireOp",EDGE,"E442"),sQuery(id+"F7.wireOp",EDGE,"E443"),sQuery(id+"F7.wireOp",EDGE,"E444"),sQuery(id+"F7.wireOp",EDGE,"E445"),sQuery(id+"F7.wireOp",EDGE,"E446"),sQuery(id+"F7.wireOp",EDGE,"E447"),sQuery(id+"F7.wireOp",EDGE,"E448"),sQuery(id+"F7.wireOp",EDGE,"E449"),sQuery(id+"F7.wireOp",EDGE,"E450"),sQuery(id+"F7.wireOp",EDGE,"E451"),sQuery(id+"F7.wireOp",EDGE,"E452"),sQuery(id+"F7.wireOp",EDGE,"E453"),sQuery(id+"F7.wireOp",EDGE,"E454"),sQuery(id+"F7.wireOp",EDGE,"E455"),sQuery(id+"F7.wireOp",EDGE,"E456"),sQuery(id+"F7.wireOp",EDGE,"E457"),sQuery(id+"F7.wireOp",EDGE,"E458"),sQuery(id+"F7.wireOp",EDGE,"E459"),sQuery(id+"F7.wireOp",EDGE,"E460"),sQuery(id+"F7.wireOp",EDGE,"E461"),sQuery(id+"F7.wireOp",EDGE,"E462"),sQuery(id+"F7.wireOp",EDGE,"E463"),sQuery(id+"F7.wireOp",EDGE,"E464"),sQuery(id+"F7.wireOp",EDGE,"E465"),sQuery(id+"F7.wireOp",EDGE,"E466"),sQuery(id+"F7.wireOp",EDGE,"E467"),sQuery(id+"F7.wireOp",EDGE,"E468"),sQuery(id+"F7.wireOp",EDGE,"E469"),sQuery(id+"F7.wireOp",EDGE,"E470"),sQuery(id+"F7.wireOp",EDGE,"E471"),sQuery(id+"F7.wireOp",EDGE,"E472"),sQuery(id+"F7.wireOp",EDGE,"E473"),sQuery(id+"F7.wireOp",EDGE,"E474"),sQuery(id+"F7.wireOp",EDGE,"E475"),sQuery(id+"F7.wireOp",EDGE,"E476"),sQuery(id+"F7.wireOp",EDGE,"E477"),sQuery(id+"F7.wireOp",EDGE,"E478"),sQuery(id+"F7.wireOp",EDGE,"E479"),sQuery(id+"F7.wireOp",EDGE,"E480"),sQuery(id+"F7.wireOp",EDGE,"E481"),sQuery(id+"F7.wireOp",EDGE,"E482"),sQuery(id+"F7.wireOp",EDGE,"E483"),sQuery(id+"F7.wireOp",EDGE,"E484"),sQuery(id+"F7.wireOp",EDGE,"E485"),sQuery(id+"F7.wireOp",EDGE,"E486"),sQuery(id+"F7.wireOp",EDGE,"E487"),sQuery(id+"F7.wireOp",EDGE,"E488"),sQuery(id+"F7.wireOp",EDGE,"E489"),sQuery(id+"F7.wireOp",EDGE,"E490"),sQuery(id+"F7.wireOp",EDGE,"E491"),sQuery(id+"F7.wireOp",EDGE,"E492"),sQuery(id+"F7.wireOp",EDGE,"E493"),sQuery(id+"F7.wireOp",EDGE,"E494"),sQuery(id+"F7.wireOp",EDGE,"E495"),sQuery(id+"F7.wireOp",EDGE,"E496"),sQuery(id+"F7.wireOp",EDGE,"E497"),sQuery(id+"F7.wireOp",EDGE,"E498"),sQuery(id+"F7.wireOp",EDGE,"E499"),sQuery(id+"F7.wireOp",EDGE,"E500"),sQuery(id+"F7.wireOp",EDGE,"E501"),sQuery(id+"F7.wireOp",EDGE,"E502"),sQuery(id+"F7.wireOp",EDGE,"E503"),sQuery(id+"F7.wireOp",EDGE,"E504"),sQuery(id+"F7.wireOp",EDGE,"E505"),sQuery(id+"F7.wireOp",EDGE,"E506"),sQuery(id+"F7.wireOp",EDGE,"E507"),sQuery(id+"F7.wireOp",EDGE,"E508"),sQuery(id+"F7.wireOp",EDGE,"E509"),sQuery(id+"F7.wireOp",EDGE,"E510"),sQuery(id+"F7.wireOp",EDGE,"E511"),sQuery(id+"F7.wireOp",EDGE,"E512"),sQuery(id+"F7.wireOp",EDGE,"E513"),sQuery(id+"F7.wireOp",EDGE,"E514"),sQuery(id+"F7.wireOp",EDGE,"E515"),sQuery(id+"F7.wireOp",EDGE,"E516"),sQuery(id+"F7.wireOp",EDGE,"E517"),sQuery(id+"F7.wireOp",EDGE,"E518"),sQuery(id+"F7.wireOp",EDGE,"E519"),sQuery(id+"F7.wireOp",EDGE,"E520"),sQuery(id+"F7.wireOp",EDGE,"E521"),sQuery(id+"F7.wireOp",EDGE,"E522"),sQuery(id+"F7.wireOp",EDGE,"E523"),sQuery(id+"F7.wireOp",EDGE,"E524"),sQuery(id+"F7.wireOp",EDGE,"E525"),sQuery(id+"F7.wireOp",EDGE,"E526"),sQuery(id+"F7.wireOp",EDGE,"E527"),sQuery(id+"F7.wireOp",EDGE,"E528"),sQuery(id+"F7.wireOp",EDGE,"E529"),sQuery(id+"F7.wireOp",EDGE,"E530"),sQuery(id+"F7.wireOp",EDGE,"E531"),sQuery(id+"F7.wireOp",EDGE,"E532"),sQuery(id+"F7.wireOp",EDGE,"E533"),sQuery(id+"F7.wireOp",EDGE,"E534"),sQuery(id+"F7.wireOp",EDGE,"E535"),sQuery(id+"F7.wireOp",EDGE,"E536"),sQuery(id+"F7.wireOp",EDGE,"E537"),sQuery(id+"F7.wireOp",EDGE,"E538"),sQuery(id+"F7.wireOp",EDGE,"E539"),sQuery(id+"F7.wireOp",EDGE,"E540"),sQuery(id+"F7.wireOp",EDGE,"E541"),sQuery(id+"F7.wireOp",EDGE,"E542"),sQuery(id+"F7.wireOp",EDGE,"E543"),sQuery(id+"F7.wireOp",EDGE,"E544"),sQuery(id+"F7.wireOp",EDGE,"E545"),sQuery(id+"F7.wireOp",EDGE,"E546"),sQuery(id+"F7.wireOp",EDGE,"E547"),sQuery(id+"F7.wireOp",EDGE,"E548"),sQuery(id+"F7.wireOp",EDGE,"E549"),sQuery(id+"F7.wireOp",EDGE,"E550"),sQuery(id+"F7.wireOp",EDGE,"E551"),sQuery(id+"F7.wireOp",EDGE,"E552"),sQuery(id+"F7.wireOp",EDGE,"E553"),sQuery(id+"F7.wireOp",EDGE,"E554"),sQuery(id+"F7.wireOp",EDGE,"E555"),sQuery(id+"F7.wireOp",EDGE,"E556"),sQuery(id+"F7.wireOp",EDGE,"E557"),sQuery(id+"F7.wireOp",EDGE,"E558"),sQuery(id+"F7.wireOp",EDGE,"E559"),sQuery(id+"F7.wireOp",EDGE,"E560"),sQuery(id+"F7.wireOp",EDGE,"E561"),sQuery(id+"F7.wireOp",EDGE,"E562"),sQuery(id+"F7.wireOp",EDGE,"E563"),sQuery(id+"F7.wireOp",EDGE,"E564"),sQuery(id+"F7.wireOp",EDGE,"E565"),sQuery(id+"F7.wireOp",EDGE,"E566"),sQuery(id+"F7.wireOp",EDGE,"E567"),sQuery(id+"F7.wireOp",EDGE,"E568"),sQuery(id+"F7.wireOp",EDGE,"E569"),sQuery(id+"F7.wireOp",EDGE,"E570"),sQuery(id+"F7.wireOp",EDGE,"E571"),sQuery(id+"F7.wireOp",EDGE,"E572"),sQuery(id+"F7.wireOp",EDGE,"E575"),sQuery(id+"F7.wireOp",EDGE,"E576"),sQuery(id+"F7.wireOp",EDGE,"E577")])],"isStart":false});
            var sketch = newSketch(context, id + "F9", { "sketchPlane" : qUnion([Q0])});
            skLineSegment(sketch, "E578.bottom", {"start": v(-26, -41) * mm, "end": v(174, -41) * mm});
            skLineSegment(sketch, "E578.top", {"start": v(-26, -291) * mm, "end": v(74, -291) * mm});
            skLineSegment(sketch, "E578.left", {"start": v(-26, -41) * mm, "end": v(-26, -291) * mm});
            skLineSegment(sketch, "E578.right", {"start": v(74, -33.1) * mm, "end": v(74, -291) * mm});
            skLineSegment(sketch, "E579.0", {"start": v(-14.75, -3.1) * mm, "end": v(70.75, -3.1) * mm});
            skLineSegment(sketch, "E580.0", {"start": v(-37, -22.39) * mm, "end": v(-37, -303.34) * mm});
            skSolve(sketch);
        }
        {
            var Q0;
            Q0=makeQuery(id+"F9.imprint","IMPRINT",FACE,{"disambiguationData":[TD([[makeQuery(id+"F9.imprint","IMPRINT",EDGE,{"derivedFrom":makeQuery(id+"F8.opExtrude","CAP_EDGE",EDGE,{"disambiguationData":[OSD([sQuery(id+"F7.wireOp",EDGE,"E490")])],"isStart":false})}),-1.0]])]});
            var Q1;
            Q1=makeQuery(id+"F9.imprint","IMPRINT",FACE,{"disambiguationData":[TD([[makeQuery(id+"F9.imprint","IMPRINT",EDGE,{"derivedFrom":makeQuery(id+"F8.opExtrude","CAP_EDGE",EDGE,{"disambiguationData":[OSD([sQuery(id+"F7.wireOp",EDGE,"E504")])],"isStart":false})}),1.0]])]});
            var Q2;
            Q2=makeQuery(id+"F9.imprint","IMPRINT",FACE,{"disambiguationData":[TD([[makeQuery(id+"F9.imprint","IMPRINT",EDGE,{"derivedFrom":makeQuery(id+"F8.opExtrude","CAP_EDGE",EDGE,{"disambiguationData":[OSD([sQuery(id+"F7.wireOp",EDGE,"E498")])],"isStart":false})}),1.0]])]});
            var Q3;
            Q3=makeQuery(id+"F9.imprint","IMPRINT",FACE,{"disambiguationData":[TD([[makeQuery(id+"F9.imprint","IMPRINT",EDGE,{"derivedFrom":makeQuery(id+"F8.opExtrude","CAP_EDGE",EDGE,{"disambiguationData":[OSD([sQuery(id+"F7.wireOp",EDGE,"E491")])],"isStart":false})}),1.0]])]});
            var Q4;
            Q4=makeQuery(id+"F9.imprint","IMPRINT",FACE,{"disambiguationData":[TD([[makeQuery(id+"F9.imprint","IMPRINT",EDGE,{"derivedFrom":makeQuery(id+"F8.opExtrude","CAP_EDGE",EDGE,{"disambiguationData":[OSD([sQuery(id+"F7.wireOp",EDGE,"E490")])],"isStart":false})}),1.0]])]});
            var Q5;
            {var subQ6=makeQuery(id+"F8.opExtrude","CAP_EDGE",EDGE,{"disambiguationData":[OSD([sQuery(id+"F7.wireOp",EDGE,"E492")])],"isStart":false});Q5=makeQuery(id+"F9.imprint","IMPRINT",FACE,{"disambiguationData":[TD([[makeQuery(id+"F9.imprint","IMPRINT",EDGE,{"derivedFrom":subQ6}),1.0]])]});}
            var Q6;
            Q6=makeQuery(id+"F9.imprint","IMPRINT",FACE,{"disambiguationData":[TD([[makeQuery(id+"F9.imprint","IMPRINT",EDGE,{"derivedFrom":makeQuery(id+"F8.opExtrude","CAP_EDGE",EDGE,{"disambiguationData":[OSD([sQuery(id+"F7.wireOp",EDGE,"E541")])],"isStart":false})}),-1.0]])]});
            var Q7;
            Q7=makeQuery(id+"F9.imprint","IMPRINT",FACE,{"disambiguationData":[TD([[makeQuery(id+"F9.imprint","IMPRINT",EDGE,{"derivedFrom":makeQuery(id+"F8.opExtrude","CAP_EDGE",EDGE,{"disambiguationData":[OSD([sQuery(id+"F7.wireOp",EDGE,"E542")])],"isStart":false})}),-1.0]])]});
            var Q8;
            Q8=makeQuery(id+"F9.imprint","IMPRINT",FACE,{"disambiguationData":[TD([[makeQuery(id+"F9.imprint","IMPRINT",EDGE,{"derivedFrom":makeQuery(id+"F8.opExtrude","CAP_EDGE",EDGE,{"disambiguationData":[OSD([sQuery(id+"F7.wireOp",EDGE,"E543")])],"isStart":false})}),-1.0]])]});
            var Q9;
            Q9=makeQuery(id+"F9.imprint","IMPRINT",FACE,{"disambiguationData":[TD([[makeQuery(id+"F9.imprint","IMPRINT",EDGE,{"derivedFrom":makeQuery(id+"F8.opExtrude","CAP_EDGE",EDGE,{"disambiguationData":[OSD([sQuery(id+"F7.wireOp",EDGE,"E544")])],"isStart":false})}),-1.0]])]});
            var Q10;
            Q10=makeQuery(id+"F9.imprint","IMPRINT",FACE,{"disambiguationData":[TD([[makeQuery(id+"F9.imprint","IMPRINT",EDGE,{"derivedFrom":makeQuery(id+"F8.opExtrude","CAP_EDGE",EDGE,{"disambiguationData":[OSD([sQuery(id+"F7.wireOp",EDGE,"E545")])],"isStart":false})}),-1.0]])]});
            var Q11;
            Q11=makeQuery(id+"F9.imprint","IMPRINT",FACE,{"disambiguationData":[TD([[makeQuery(id+"F9.imprint","IMPRINT",EDGE,{"derivedFrom":makeQuery(id+"F8.opExtrude","CAP_EDGE",EDGE,{"disambiguationData":[OSD([sQuery(id+"F7.wireOp",EDGE,"E546")])],"isStart":false})}),-1.0]])]});
            var Q12;
            Q12=makeQuery(id+"F9.imprint","IMPRINT",FACE,{"disambiguationData":[TD([[makeQuery(id+"F9.imprint","IMPRINT",EDGE,{"derivedFrom":makeQuery(id+"F8.opExtrude","CAP_EDGE",EDGE,{"disambiguationData":[OSD([sQuery(id+"F7.wireOp",EDGE,"E547")])],"isStart":false})}),-1.0]])]});
            var Q13;
            {var subQ0=makeQuery(id+"F8.opExtrude","CAP_EDGE",EDGE,{"disambiguationData":[OSD([sQuery(id+"F7.wireOp",EDGE,"E501")])],"isStart":false});Q13=makeQuery(id+"F9.imprint","IMPRINT",FACE,{"disambiguationData":[TD([[makeQuery(id+"F9.imprint","IMPRINT",EDGE,{"derivedFrom":subQ0}),1.0]])]});}
            var Q14;
            {var subQ4=makeQuery(id+"F8.opExtrude","CAP_EDGE",EDGE,{"disambiguationData":[OSD([sQuery(id+"F7.wireOp",EDGE,"E507")])],"isStart":false});Q14=makeQuery(id+"F9.imprint","IMPRINT",FACE,{"disambiguationData":[TD([[makeQuery(id+"F9.imprint","IMPRINT",EDGE,{"derivedFrom":subQ4}),1.0]])]});}
            var Q15;
            {var subQ1=makeQuery(id+"F8.opExtrude","CAP_EDGE",EDGE,{"disambiguationData":[OSD([sQuery(id+"F7.wireOp",EDGE,"E495")])],"isStart":false});Q15=makeQuery(id+"F9.imprint","IMPRINT",FACE,{"disambiguationData":[TD([[makeQuery(id+"F9.imprint","IMPRINT",EDGE,{"derivedFrom":subQ1}),1.0]])]});}
            var Q16;
            {var subQ5=makeQuery(id+"F8.opExtrude","CAP_EDGE",EDGE,{"disambiguationData":[OSD([sQuery(id+"F7.wireOp",EDGE,"E555")])],"isStart":false});Q16=makeQuery(id+"F9.imprint","IMPRINT",FACE,{"disambiguationData":[TD([[makeQuery(id+"F9.imprint","IMPRINT",EDGE,{"derivedFrom":subQ5}),1.0]])]});}
            var Q17;
            {var subQ5=makeQuery(id+"F8.opExtrude","CAP_EDGE",EDGE,{"disambiguationData":[OSD([sQuery(id+"F7.wireOp",EDGE,"E556")])],"isStart":false});Q17=makeQuery(id+"F9.imprint","IMPRINT",FACE,{"disambiguationData":[TD([[makeQuery(id+"F9.imprint","IMPRINT",EDGE,{"derivedFrom":subQ5}),1.0]])]});}
            extrude(context, id + "F10", {"entities" : qUnion([Q0, Q1, Q2, Q3, Q4, Q5, Q6, Q7, Q8, Q9, Q10, Q11, Q12, Q13, Q14, Q15, Q16, Q17]), "depth" : (getVariable(context, 'profondeur_alim')) * mm, "offsetDistance" : 25 * mm});
        }
    });
